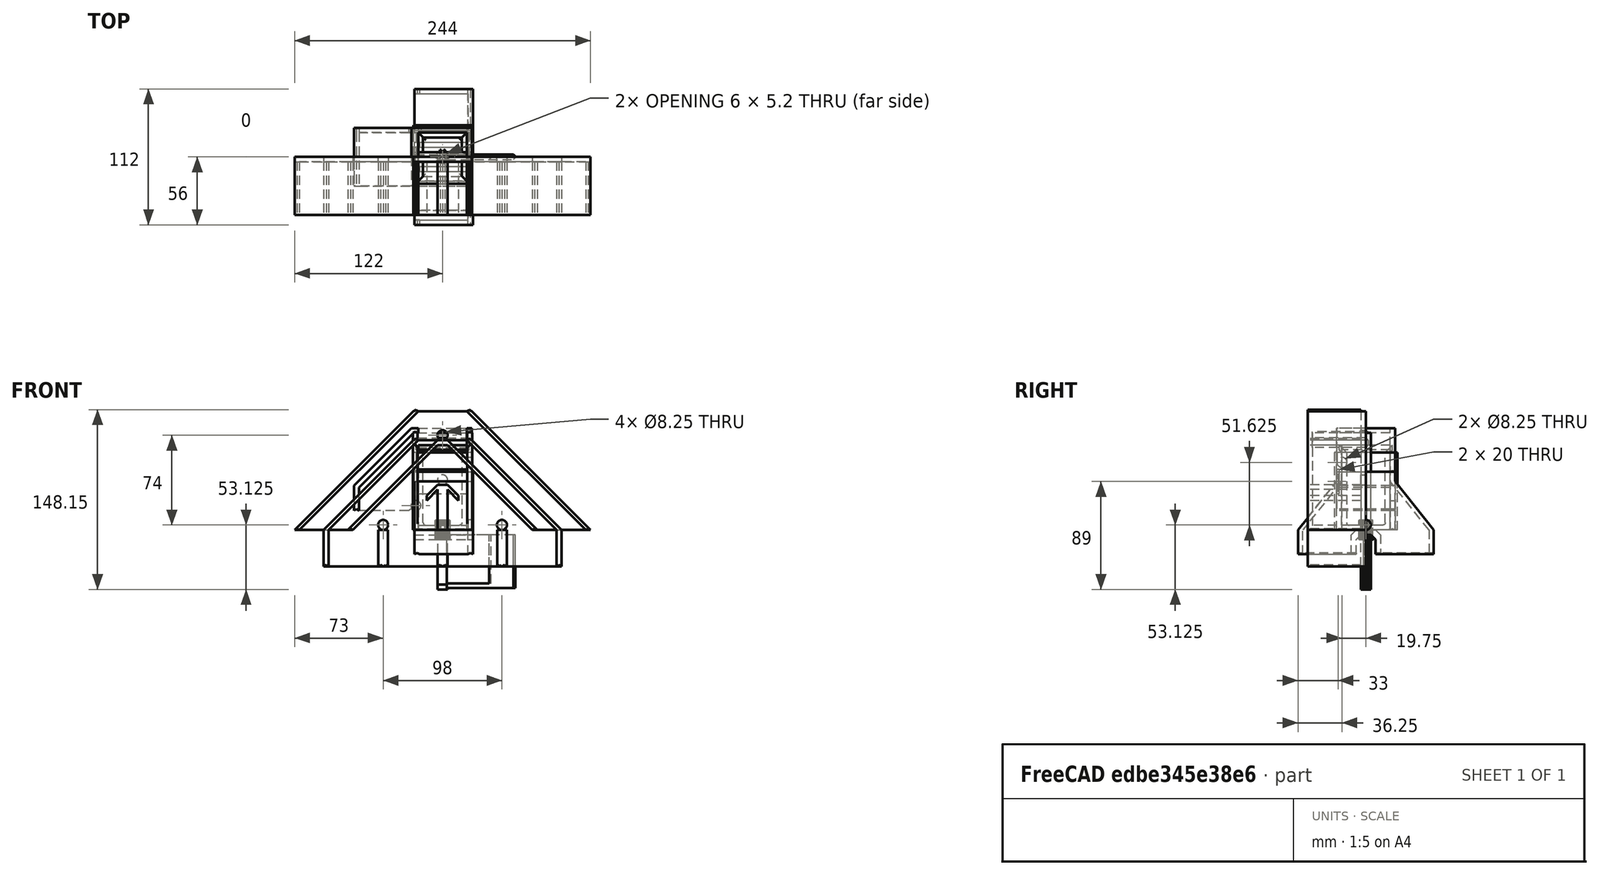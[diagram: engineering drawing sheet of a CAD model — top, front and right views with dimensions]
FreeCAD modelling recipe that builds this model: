
FCSTD DOCUMENT  (FreeCAD 1.0R39319 (Git))
Label: Sorter
License: GNU GPLv3
LicenseURL: https://www.gnu.org/licenses/gpl-3.0.en.html
objects: App::Link×58, Part::Extrusion×27, Sketcher::SketchObject×26, Part::MultiFuse×8, Part::Cut×4, Part::Fuse×2, Part::Fillet×2, Part::Chamfer×2, Spreadsheet::Sheet×1, Part::Part2DObjectPython×1, App::FeaturePython×1, Assembly::JointGroup×1, Assembly::AssemblyObject×1
note: 98 computed .brp shape members not serialized (recipe doc carries the construction recipe); baked Part::Feature solids carry a one-line shape summary decoded from their .brp

FEATURE [Spreadsheet::Sheet] Spreadsheet  label="Variables"
  cells = A1='Bin Width; B1(BinWidth)==40 mm; A2='Bin Height; B2(BinHeight)==60 mm; A3='Wall Width; B3(WallWidth)==4 mm; A4='Tolerance; B4(Tolerance)==1 mm; A5='Connector Angle; B5(ConnectorAngle)==30 deg; A6='Flap Pin Diameter; B6(FlapPinDiameter)==8 mm; A7='Flap Tolerance; B7(FlapTolerance)==0.25 mm
FEATURE [Sketcher::SketchObject] Sketch001
  ArcFitTolerance = 1e-06
  FullyConstrained = true
  MakeInternals = false
  MapMode = 2
  Placement = pos=(0,0,0) rot=(1,0,0;1.5708rad)
  expr: Constraints[16] = <<Variables>>.BinWidth + <<Variables>>.Tolerance
  expr: Constraints[19] = <<Variables>>.WallWidth
  expr: Constraints[20] = <<Variables>>.WallWidth
  expr: Constraints[21] = <<Variables>>.BinHeight + <<Variables>>.WallWidth
  expr: Constraints[30] = <<Variables>>.WallWidth
  expr: Constraints[31] = <<Variables>>.WallWidth
  expr: Constraints[32] = <<Variables>>.WallWidth
  expr: Constraints[33] = <<Variables>>.WallWidth / 2
  expr: Constraints[54] = <<Variables>>.ConnectorAngle
  sketch-geometry (20):
    g0: LineSegment StartX=24.5 StartY=0 StartZ=0 EndX=-24.5 EndY=0 EndZ=0
    g1: LineSegment StartX=-24.5 StartY=0 StartZ=0 EndX=-24.5 EndY=80 EndZ=0
    g2: LineSegment StartX=-20.5 StartY=80 StartZ=0 EndX=-20.5 EndY=76 EndZ=0
    g3: LineSegment StartX=-20.5 StartY=76 StartZ=0 EndX=-22.5 EndY=74 EndZ=0
    g4: LineSegment StartX=-22.5 StartY=74 StartZ=0 EndX=-22.5 EndY=70 EndZ=0
    g5: LineSegment StartX=-22.5 StartY=70 StartZ=0 EndX=-20.5 EndY=68 EndZ=0
    g6: LineSegment StartX=-20.5 StartY=68 StartZ=0 EndX=-20.5 EndY=4 EndZ=0
    g7: LineSegment StartX=-20.5 StartY=4 StartZ=0 EndX=20.5 EndY=4 EndZ=0
    g8: LineSegment StartX=20.5 StartY=4 StartZ=0 EndX=20.5 EndY=68 EndZ=0
    g9: LineSegment StartX=20.5 StartY=68 StartZ=0 EndX=22.5 EndY=70 EndZ=0
    g10: LineSegment StartX=22.5 StartY=70 StartZ=0 EndX=22.5 EndY=74 EndZ=0
    g11: LineSegment StartX=22.5 StartY=74 StartZ=0 EndX=20.5 EndY=76 EndZ=0
    g12: LineSegment StartX=20.5 StartY=76 StartZ=0 EndX=20.5 EndY=80 EndZ=0
    g13: LineSegment StartX=24.5 StartY=80 StartZ=0 EndX=24.5 EndY=0 EndZ=0
    g14: LineSegment StartX=20.5 StartY=80 StartZ=0 EndX=22.5 EndY=81.1547 EndZ=0
    g15: LineSegment StartX=22.5 StartY=81.1547 StartZ=0 EndX=24.5 EndY=80 EndZ=0
    g16: LineSegment [constr] StartX=20.5 StartY=80 StartZ=0 EndX=24.5 EndY=80 EndZ=0
    g17: LineSegment StartX=-24.5 StartY=80 StartZ=0 EndX=-22.5 EndY=81.1547 EndZ=0
    g18: LineSegment StartX=-22.5 StartY=81.1547 StartZ=0 EndX=-20.5 EndY=80 EndZ=0
    g19: LineSegment [constr] StartX=-24.5 StartY=80 StartZ=0 EndX=-20.5 EndY=80 EndZ=0
  constraints (56):
    c: Coincident(g0,g1)
    c: Vertical(g1)
    c: Vertical(g2)
    c: Vertical(g4)
    c: Coincident(g5,g6)
    c: Vertical(g6)
    c: Coincident(g6,g7)
    c: Coincident(g7,g8)
    c: Vertical(g8)
    c: Coincident(g8,g9)
    c: Coincident(g9,g10)
    c: Vertical(g10)
    c: Coincident(g10,g11)
    c: Coincident(g11,g12)
    c: Coincident(g13,g0)
    c: Vertical(g13)
    c: DistanceX(g7,g7) = 41
    c: Symmetric(g0,g0,g-2)
    c: Symmetric(g7,g6,g-2)
    c: DistanceX(g7,g0) = 4
    c: DistanceY(g0,g7) = 4
    c: DistanceY(g8,g8) = 64
    c: Equal(g6,g8)
    c: Equal(g13,g1)
    c: Equal(g2,g12)
    c: Vertical(g12)
    c: Angle(g8,g9) = 2.35619
    c: Angle(g11,g12) = 2.35619
    c: Angle(g5,g6) = 2.35619
    c: Angle(g2,g3) = 2.35619
    c: DistanceX(g12,g13) = 4
    c: DistanceY(g12,g12) = 4
    c: DistanceY(g10,g10) = 4
    c: DistanceX(g9,g13) = 2
    c: Equal(g4,g10)
    c: PointOnObject(g0,g-1)
    c: Coincident(g12,g14)
    c: Coincident(g14,g15)
    c: Coincident(g15,g13)
    c: Equal(g14,g15)
    c: Coincident(g16,g12)
    c: Coincident(g16,g13)
    c: Horizontal(g16)
    c: Coincident(g1,g17)
    c: Coincident(g17,g18)
    c: Coincident(g18,g2)
    c: Equal(g17,g18)
    c: Coincident(g19,g1)
    c: Coincident(g19,g2)
    c: Horizontal(g19)
    c: Coincident(g3,g2)
    c: Coincident(g3,g4)
    c: Coincident(g4,g5)
    c: Equal(g19,g16)
    c: Angle(g19,g17) = 0.523599
    c: Parallel(g14,g17)
FEATURE [Sketcher::SketchObject] Sketch002
  ArcFitTolerance = 1e-06
  AttachmentSupport = -> [Sketch001]
  FullyConstrained = true
  MakeInternals = false
  MapMode = 4
  Placement = pos=(0,0,0) rot=(0.707107,0,0.707107;3.14159rad)
  expr: Constraints[21] = <<Variables>>.WallWidth
  expr: Constraints[22] = <<Variables>>.WallWidth
  expr: Constraints[23] = <<Variables>>.WallWidth / 2
  expr: Constraints[25] = <<Variables>>.BinHeight + <<Variables>>.WallWidth * 2
  expr: Constraints[6] = <<Variables>>.WallWidth
  sketch-geometry (9):
    g0: LineSegment StartX=0 StartY=0 StartZ=0 EndX=0 EndY=-4 EndZ=0
    g1: LineSegment StartX=0 StartY=-4 StartZ=0 EndX=68 EndY=-4 EndZ=0
    g2: LineSegment StartX=68 StartY=0 StartZ=0 EndX=0 EndY=0 EndZ=0
    g3: LineSegment StartX=68 StartY=0 StartZ=0 EndX=70 EndY=-2 EndZ=0
    g4: LineSegment StartX=70 StartY=-2 StartZ=0 EndX=74 EndY=-2 EndZ=0
    g5: LineSegment StartX=74 StartY=-2 StartZ=0 EndX=76 EndY=0 EndZ=0
    g6: LineSegment StartX=76 StartY=0 StartZ=0 EndX=80 EndY=0 EndZ=0
    g7: LineSegment StartX=80 StartY=0 StartZ=0 EndX=80 EndY=-4 EndZ=0
    g8: LineSegment StartX=80 StartY=-4 StartZ=0 EndX=68 EndY=-4 EndZ=0
  constraints (26):
    c: Coincident(g-1,g0)
    c: PointOnObject(g0,g-2)
    c: Coincident(g0,g1)
    c: Horizontal(g1)
    c: PointOnObject(g2,g-1)
    c: Coincident(g2,g0)
    c: DistanceY(g0,g0) = 4
    c: Coincident(g2,g3)
    c: Coincident(g3,g4)
    c: Coincident(g4,g5)
    c: PointOnObject(g5,g-1)
    c: Coincident(g5,g6)
    c: PointOnObject(g6,g-1)
    c: Coincident(g6,g7)
    c: Vertical(g7)
    c: Coincident(g7,g8)
    c: Coincident(g8,g1)
    c: Horizontal(g8)
    c: Horizontal(g4)
    c: Angle(g2,g3) = 2.35619
    c: Angle(g5,g6) = 2.35619
    c: DistanceX(g6,g6) = 4
    c: DistanceX(g4,g4) = 4
    c: DistanceY(g7,g3) = 2
    c: Equal(g2,g1)
    c: DistanceX(g2,g2) = 68
FEATURE [Part::Extrusion] Extrude
  Base = -> Sketch001
  Dir = (0,-1,2e-16)
  DirMode = 2
  FaceMakerClass = Part::FaceMakerBullseye
  FaceMakerMode = 3
  LengthFwd = 46
  LengthRev = 0
  Placement = pos=(0,2,0) rot=(0,0,1;0rad)
  Solid = true
  Symmetric = false
  expr: .Placement.Base.y = <<Variables>>.WallWidth / 2
  expr: LengthFwd = <<Variables>>.BinWidth + <<Variables>>.WallWidth * 1.5
FEATURE [Part::Extrusion] Extrude001
  Base = -> Sketch002
  Dir = (1,0,-2e-16)
  DirMode = 2
  FaceMakerClass = Part::FaceMakerBullseye
  FaceMakerMode = 3
  LengthFwd = 49
  LengthRev = 0
  Solid = true
  Symmetric = true
  expr: LengthFwd = <<Variables>>.BinWidth + <<Variables>>.Tolerance + <<Variables>>.WallWidth * 2
FEATURE [Sketcher::SketchObject] Sketch003
  ArcFitTolerance = 1e-06
  FullyConstrained = true
  MakeInternals = false
  Placement = pos=(0,0,0) rot=(1,0,0;1.5708rad)
  expr: Constraints[11] = <<Variables>>.BinWidth
  expr: Constraints[12] = <<Variables>>.WallWidth
  expr: Constraints[13] = <<Variables>>.WallWidth
  expr: Constraints[16] = <<Variables>>.BinHeight + <<Variables>>.WallWidth
  expr: Constraints[31] = <<Variables>>.WallWidth
  expr: Constraints[33] = <<Variables>>.WallWidth / 2
  sketch-geometry (12):
    g0: LineSegment StartX=-20 StartY=0 StartZ=0 EndX=20 EndY=0 EndZ=0
    g1: LineSegment StartX=20 StartY=0 StartZ=0 EndX=20 EndY=64 EndZ=0
    g2: LineSegment StartX=20 StartY=64 StartZ=0 EndX=22 EndY=66 EndZ=0
    g3: LineSegment StartX=16 StartY=64 StartZ=0 EndX=16 EndY=4 EndZ=0
    g4: LineSegment StartX=16 StartY=4 StartZ=0 EndX=-16 EndY=4 EndZ=0
    g5: LineSegment StartX=-16 StartY=4 StartZ=0 EndX=-16 EndY=64 EndZ=0
    g6: LineSegment StartX=-22 StartY=66 StartZ=0 EndX=-20 EndY=64 EndZ=0
    g7: LineSegment StartX=-20 StartY=64 StartZ=0 EndX=-20 EndY=0 EndZ=0
    g8: LineSegment StartX=22 StartY=66 StartZ=0 EndX=22 EndY=70 EndZ=0
    g9: LineSegment StartX=16 StartY=64 StartZ=0 EndX=22 EndY=70 EndZ=0
    g10: LineSegment StartX=-22 StartY=66 StartZ=0 EndX=-22 EndY=70 EndZ=0
    g11: LineSegment StartX=-22 StartY=70 StartZ=0 EndX=-16 EndY=64 EndZ=0
  constraints (34):
    c: PointOnObject(g0,g-1)
    c: Coincident(g0,g1)
    c: Vertical(g1)
    c: Coincident(g1,g2)
    c: Vertical(g3)
    c: Coincident(g3,g4)
    c: Coincident(g4,g5)
    c: Vertical(g5)
    c: Coincident(g6,g7)
    c: Coincident(g7,g0)
    c: Vertical(g7)
    c: DistanceX(g0,g0) = 40
    c: DistanceY(g0,g4) = 4
    c: DistanceX(g0,g4) = 4
    c: Symmetric(g0,g0,g-2)
    c: Symmetric(g4,g3,g-2)
    c: DistanceY(g1,g1) = 64
    c: Equal(g5,g3)
    c: Equal(g7,g1)
    c: Angle(g1,g2) = 2.35619
    c: Angle(g6,g7) = 2.35619
    c: Coincident(g2,g8)
    c: Vertical(g8)
    c: Coincident(g3,g9)
    c: Coincident(g9,g8)
    c: Coincident(g6,g10)
    c: Vertical(g10)
    c: Coincident(g10,g11)
    c: Coincident(g11,g5)
    c: Angle(g11,g5) = 2.35619
    c: Angle(g3,g9) = 2.35619
    c: DistanceY(g10,g10) = 4
    c: Equal(g9,g11)
    c: DistanceX(g6,g6) = 2
FEATURE [Part::Extrusion] Extrude002
  Base = -> Sketch003
  Dir = (0,-1,2e-16)
  DirMode = 2
  FaceMakerClass = Part::FaceMakerBullseye
  FaceMakerMode = 3
  LengthFwd = 40
  LengthRev = 0
  Solid = true
  Symmetric = true
  expr: LengthFwd = <<Variables>>.BinWidth
FEATURE [Part::Fuse] Fusion  label="Union001"
  Base = -> Extrude
  Tool = -> Extrude001
FEATURE [Sketcher::SketchObject] Sketch004
  ArcFitTolerance = 1e-06
  AttachmentSupport = -> [Extrude002]
  FullyConstrained = true
  MakeInternals = false
  MapMode = 4
  Placement = pos=(0,0,0) rot=(0.57735,0.57735,0.57735;2.0944rad)
  expr: Constraints[17] = <<Variables>>.BinWidth
  expr: Constraints[18] = <<Variables>>.BinHeight + <<Variables>>.WallWidth
  expr: Constraints[19] = <<Variables>>.WallWidth
  expr: Constraints[20] = <<Variables>>.WallWidth
  expr: Constraints[21] = <<Variables>>.WallWidth / 2
  expr: Constraints[30] = <<Variables>>.WallWidth
  sketch-geometry (12):
    g0: LineSegment StartX=20 StartY=0 StartZ=0 EndX=-20 EndY=0 EndZ=0
    g1: LineSegment StartX=-20 StartY=0 StartZ=0 EndX=-20 EndY=64 EndZ=0
    g2: LineSegment StartX=-20 StartY=64 StartZ=0 EndX=-22 EndY=66 EndZ=0
    g3: LineSegment StartX=-16 StartY=64 StartZ=0 EndX=-16 EndY=4 EndZ=0
    g4: LineSegment StartX=-16 StartY=4 StartZ=0 EndX=16 EndY=4 EndZ=0
    g5: LineSegment StartX=16 StartY=4 StartZ=0 EndX=16 EndY=64 EndZ=0
    g6: LineSegment StartX=22 StartY=66 StartZ=0 EndX=20 EndY=64 EndZ=0
    g7: LineSegment StartX=20 StartY=64 StartZ=0 EndX=20 EndY=0 EndZ=0
    g8: LineSegment StartX=-22 StartY=66 StartZ=0 EndX=-22 EndY=70 EndZ=0
    g9: LineSegment StartX=-22 StartY=70 StartZ=0 EndX=-16 EndY=64 EndZ=0
    g10: LineSegment StartX=22 StartY=66 StartZ=0 EndX=22 EndY=70 EndZ=0
    g11: LineSegment StartX=22 StartY=70 StartZ=0 EndX=16 EndY=64 EndZ=0
  constraints (34):
    c: PointOnObject(g0,g-1)
    c: Coincident(g0,g1)
    c: Vertical(g1)
    c: Coincident(g1,g2)
    c: Vertical(g3)
    c: Coincident(g3,g4)
    c: Coincident(g4,g5)
    c: Vertical(g5)
    c: Coincident(g6,g7)
    c: Coincident(g7,g0)
    c: Vertical(g7)
    c: Symmetric(g0,g0,g-2)
    c: Symmetric(g3,g4,g-2)
    c: Angle(g2,g1) = 2.35619
    c: Angle(g7,g6) = 2.35619
    c: Equal(g3,g5)
    c: Equal(g7,g1)
    c: DistanceX(g0,g0) = 40
    c: DistanceY(g7,g7) = 64
    c: DistanceX(g4,g0) = 4
    c: DistanceY(g0,g4) = 4
    c: DistanceX(g2,g1) = 2
    c: Coincident(g2,g8)
    c: Vertical(g8)
    c: Coincident(g8,g9)
    c: Coincident(g9,g3)
    c: Coincident(g6,g10)
    c: Vertical(g10)
    c: Coincident(g10,g11)
    c: Coincident(g11,g5)
    c: DistanceY(g8,g8) = 4
    c: Angle(g9,g3) = 2.35619
    c: Angle(g5,g11) = 2.35619
    c: Equal(g6,g2)
FEATURE [Part::Extrusion] Extrude003
  Base = -> Sketch004
  Dir = (1,0,0)
  DirMode = 2
  FaceMakerClass = Part::FaceMakerBullseye
  FaceMakerMode = 3
  LengthFwd = 40
  LengthRev = 0
  Solid = true
  Symmetric = true
  expr: LengthFwd = <<Variables>>.BinWidth
FEATURE [Part::Fuse] Fusion001  label="Union"
  Base = -> Extrude002
  Tool = -> Extrude003
FEATURE [Part::Fillet] Fillet  label="Bin"
  Base = -> Fusion001
  EdgeLinks = -> Fusion001 [Edge11,Edge21,Edge23,Edge30,Edge31,Edge44,Edge50,Edge51,Edge69,Edge73,Edge75,Edge77]
  Edges = 12 edges r=2: [Edge11,Edge21,Edge23,Edge30,Edge31,Edge44,Edge50,Edge51,Edge69,Edge73,Edge75,Edge77]
FEATURE [Part::Fillet] Fillet001  label="Bin Holder"
  Base = -> Fusion
  EdgeLinks = -> Fusion [Edge72,Edge73,Edge74]
  Edges = 3 edges r=1: [Edge72,Edge73,Edge74]
FEATURE [Sketcher::SketchObject] Sketch
  ArcFitTolerance = 1e-06
  FullyConstrained = true
  MakeInternals = false
  MapMode = 5
  Placement = pos=(0,0,0) rot=(1,0,0;1.5708rad)
  expr: Constraints[144] = <<Variables>>.ConnectorAngle
  expr: Constraints[17] = <<Variables>>.WallWidth
  expr: Constraints[29] = <<Variables>>.BinWidth + <<Variables>>.Tolerance
  expr: Constraints[2] = <<Variables>>.WallWidth * 2
  expr: Constraints[36] = <<Variables>>.WallWidth * 2
  expr: Constraints[82] = <<Variables>>.BinWidth
  expr: Constraints[87] = <<Variables>>.WallWidth
  expr: Constraints[91] = <<Variables>>.BinWidth
  expr: Constraints[95] = <<Variables>>.BinWidth
  sketch-geometry (58):
    g0: LineSegment StartX=-20 StartY=74 StartZ=0 EndX=-94 EndY=1.8e-15 EndZ=0
    g1: LineSegment StartX=24 StartY=74 StartZ=0 EndX=98 EndY=1.8e-15 EndZ=0
    g2: LineSegment StartX=4 StartY=37.3394 StartZ=0 EndX=-4 EndY=37.3394 EndZ=0
    g3: LineSegment StartX=4 StartY=37.3394 StartZ=0 EndX=13.146 EndY=28.1934 EndZ=0
    g4: LineSegment StartX=-4 StartY=37.3394 StartZ=0 EndX=-13.146 EndY=28.1934 EndZ=0
    g5: LineSegment StartX=-24 StartY=74 StartZ=0 EndX=-98 EndY=4.4e-15 EndZ=0
    g6: LineSegment StartX=94 StartY=0 StartZ=0 EndX=20 EndY=74 EndZ=0
    g7: LineSegment StartX=-13.146 StartY=24.1934 StartZ=0 EndX=-4 EndY=33.3394 EndZ=0
    g8: LineSegment StartX=4 StartY=33.3394 StartZ=0 EndX=13.146 EndY=24.1934 EndZ=0
    g9: LineSegment StartX=-13.146 StartY=24.1934 StartZ=0 EndX=-13.146 EndY=28.1934 EndZ=0
    g10: LineSegment StartX=13.146 StartY=28.1934 StartZ=0 EndX=13.146 EndY=24.1934 EndZ=0
    g11: LineSegment [constr] StartX=-94 StartY=1.8e-15 StartZ=0 EndX=-53 EndY=0 EndZ=0
    g12: LineSegment StartX=-53 StartY=0 StartZ=0 EndX=-45 EndY=0 EndZ=0
    g13: LineSegment [constr] StartX=-45 StartY=0 StartZ=0 EndX=-4 EndY=0 EndZ=0
    g14: LineSegment [constr] StartX=4 StartY=0 StartZ=0 EndX=45 EndY=0 EndZ=0
    g15: LineSegment StartX=45 StartY=0 StartZ=0 EndX=53 EndY=0 EndZ=0
    g16: LineSegment StartX=-98 StartY=4.4e-15 StartZ=0 EndX=-98 EndY=-30 EndZ=0
    g17: LineSegment [constr] StartX=-98 StartY=-30 StartZ=0 EndX=-94 EndY=-30 EndZ=0
    g18: LineSegment StartX=-94 StartY=-30 StartZ=0 EndX=-94 EndY=3.6e-15 EndZ=0
    g19: LineSegment StartX=-53 StartY=0 StartZ=0 EndX=-53 EndY=-30 EndZ=0
    g20: LineSegment [constr] StartX=-53 StartY=-30 StartZ=0 EndX=-45 EndY=-30 EndZ=0
    g21: LineSegment StartX=-45 StartY=-30 StartZ=0 EndX=-45 EndY=0 EndZ=0
    g22: LineSegment StartX=-4 StartY=0 StartZ=0 EndX=-4 EndY=-30 EndZ=0
    g23: LineSegment [constr] StartX=-4 StartY=-30 StartZ=0 EndX=4 EndY=-30 EndZ=0
    g24: LineSegment StartX=4 StartY=-30 StartZ=0 EndX=4 EndY=0 EndZ=0
    g25: LineSegment StartX=45 StartY=0 StartZ=0 EndX=45 EndY=-30 EndZ=0
    g26: LineSegment [constr] StartX=45 StartY=-30 StartZ=0 EndX=53 EndY=-30 EndZ=0
    g27: LineSegment StartX=53 StartY=-30 StartZ=0 EndX=53 EndY=0 EndZ=0
    g28: LineSegment StartX=98 StartY=1.8e-15 StartZ=0 EndX=98 EndY=-30 EndZ=0
    g29: LineSegment [constr] StartX=98 StartY=-30 StartZ=0 EndX=94 EndY=-30 EndZ=0
    g30: LineSegment StartX=94 StartY=-30 StartZ=0 EndX=94 EndY=0 EndZ=0
    g31: LineSegment [constr] StartX=-20 StartY=74 StartZ=0 EndX=20 EndY=74 EndZ=0
    g32: LineSegment [constr] StartX=20 StartY=74 StartZ=0 EndX=24 EndY=74 EndZ=0
    g33: LineSegment [constr] StartX=-24 StartY=74 StartZ=0 EndX=-20 EndY=74 EndZ=0
    g34: LineSegment [constr] StartX=4 StartY=37.3394 StartZ=0 EndX=20 EndY=74 EndZ=0
    g35: LineSegment [constr] StartX=53 StartY=0 StartZ=0 EndX=94 EndY=0 EndZ=0
    g36: LineSegment StartX=4 StartY=33.3394 StartZ=0 EndX=4 EndY=0 EndZ=0
    g37: LineSegment StartX=-4 StartY=0 StartZ=0 EndX=-4 EndY=33.3394 EndZ=0
    g38: LineSegment StartX=-98 StartY=-30 StartZ=0 EndX=-96 EndY=-28.8453 EndZ=0
    g39: LineSegment StartX=-96 StartY=-28.8453 StartZ=0 EndX=-94 EndY=-30 EndZ=0
    g40: LineSegment StartX=-53 StartY=-30 StartZ=0 EndX=-51 EndY=-28.8453 EndZ=0
    g41: LineSegment StartX=-51 StartY=-28.8453 StartZ=0 EndX=-49 EndY=-30 EndZ=0
    g42: LineSegment StartX=-49 StartY=-30 StartZ=0 EndX=-47 EndY=-28.8453 EndZ=0
    g43: LineSegment StartX=-47 StartY=-28.8453 StartZ=0 EndX=-45 EndY=-30 EndZ=0
    g44: LineSegment StartX=-4 StartY=-30 StartZ=0 EndX=-2 EndY=-28.8453 EndZ=0
    g45: LineSegment StartX=-2 StartY=-28.8453 StartZ=0 EndX=-1e-16 EndY=-30 EndZ=0
    g46: LineSegment StartX=-1e-16 StartY=-30 StartZ=0 EndX=2 EndY=-28.8453 EndZ=0
    g47: LineSegment StartX=2 StartY=-28.8453 StartZ=0 EndX=4 EndY=-30 EndZ=0
    g48: LineSegment StartX=45 StartY=-30 StartZ=0 EndX=47 EndY=-28.8453 EndZ=0
    g49: LineSegment StartX=47 StartY=-28.8453 StartZ=0 EndX=49 EndY=-30 EndZ=0
    g50: LineSegment StartX=49 StartY=-30 StartZ=0 EndX=51 EndY=-28.8453 EndZ=0
    g51: LineSegment StartX=51 StartY=-28.8453 StartZ=0 EndX=53 EndY=-30 EndZ=0
    g52: LineSegment StartX=94 StartY=-30 StartZ=0 EndX=96 EndY=-28.8453 EndZ=0
    g53: LineSegment StartX=96 StartY=-28.8453 StartZ=0 EndX=98 EndY=-30 EndZ=0
    g54: LineSegment StartX=-24 StartY=74 StartZ=0 EndX=-22 EndY=75.1547 EndZ=0
    g55: LineSegment StartX=-22 StartY=75.1547 StartZ=0 EndX=-20 EndY=74 EndZ=0
    g56: LineSegment StartX=20 StartY=74 StartZ=0 EndX=22 EndY=75.1547 EndZ=0
    g57: LineSegment StartX=22 StartY=75.1547 StartZ=0 EndX=24 EndY=74 EndZ=0
  constraints (154):
    c: PointOnObject(g0,g-1)
    c: PointOnObject(g1,g-1)
    c: DistanceX(g2,g2) = 8
    c: Symmetric(g2,g2,g-2)
    c: Coincident(g3,g2)
    c: Coincident(g4,g2)
    c: Parallel(g4,g0)
    c: Parallel(g3,g1)
    c: Perpendicular(g1,g0)
    c: Equal(g4,g3)
    c: PointOnObject(g5,g-1)
    c: Equal(g5,g0)
    c: Parallel(g0,g5)
    c: PointOnObject(g6,g-1)
    c: Parallel(g1,g6)
    c: Equal(g6,g1)
    c: Symmetric(g7,g8,g-2)
    c: Distance(g7,g2) = 4
    c: Parallel(g7,g4)
    c: Equal(g4,g7)
    c: Equal(g3,g8)
    c: Parallel(g8,g3)
    c: Coincident(g9,g7)
    c: Coincident(g9,g4)
    c: Coincident(g10,g3)
    c: Coincident(g10,g8)
    c: Vertical(g10)
    c: Coincident(g11,g0)
    c: PointOnObject(g11,g-1)
    c: DistanceX(g11,g11) = 41
    c: Coincident(g12,g11)
    c: PointOnObject(g12,g-1)
    c: Coincident(g13,g12)
    c: PointOnObject(g13,g-1)
    c: Symmetric(g13,g14,g-2)
    c: Equal(g11,g13)
    c: DistanceX(g12,g12) = 8
    c: PointOnObject(g14,g-1)
    c: Coincident(g15,g14)
    c: PointOnObject(g15,g-1)
    c: Equal(g14,g11)
    c: Coincident(g5,g16)
    c: Vertical(g16)
    c: Coincident(g16,g17)
    c: Horizontal(g17)
    c: Coincident(g17,g18)
    c: Coincident(g18,g0)
    c: Vertical(g18)
    c: Coincident(g11,g19)
    c: Vertical(g19)
    c: Coincident(g19,g20)
    c: Horizontal(g20)
    c: Coincident(g20,g21)
    c: Coincident(g21,g12)
    c: Vertical(g21)
    c: Coincident(g13,g22)
    c: Vertical(g22)
    c: Coincident(g22,g23)
    c: Horizontal(g23)
    c: Coincident(g23,g24)
    c: Vertical(g24)
    c: Coincident(g14,g25)
    c: Vertical(g25)
    c: Coincident(g25,g26)
    c: Horizontal(g26)
    c: Coincident(g26,g27)
    c: Coincident(g27,g15)
    c: Vertical(g27)
    c: Coincident(g1,g28)
    c: Vertical(g28)
    c: Coincident(g28,g29)
    c: Horizontal(g29)
    c: Coincident(g29,g30)
    c: Coincident(g30,g6)
    c: Vertical(g30)
    c: Equal(g28,g27)
    c: Equal(g25,g24)
    c: Equal(g22,g21)
    c: Equal(g19,g16)
    c: DistanceY(g16,g16) = 30
    c: Coincident(g31,g0)
    c: Coincident(g31,g6)
    c: DistanceX(g31,g31) = 40
    c: Coincident(g32,g6)
    c: Coincident(g32,g1)
    c: Coincident(g33,g5)
    c: Coincident(g33,g0)
    c: DistanceX(g33,g33) = 4
    c: Equal(g33,g32)
    c: Coincident(g34,g2)
    c: Coincident(g34,g6)
    c: Distance(g34,g34) = 40
    c: Coincident(g35,g15)
    c: Coincident(g35,g6)
    c: Equal(g14,g35)
    c: Distance(g8,g14) = 40
    c: Symmetric(g6,g0,g-2)
    c: Coincident(g37,g13)
    c: Coincident(g37,g7)
    c: Coincident(g36,g14)
    c: Coincident(g24,g14)
    c: Vertical(g37)
    c: Equal(g12,g15)
    c: Coincident(g36,g8)
    c: Coincident(g16,g38)
    c: Coincident(g38,g39)
    c: Coincident(g39,g17)
    c: Coincident(g19,g40)
    c: Coincident(g40,g41)
    c: Symmetric(g20,g20,g41)
    c: Coincident(g41,g42)
    c: Coincident(g42,g43)
    c: Coincident(g43,g20)
    c: Coincident(g22,g44)
    c: Coincident(g44,g45)
    c: Symmetric(g23,g23,g45)
    c: Coincident(g45,g46)
    c: Coincident(g46,g47)
    c: Coincident(g47,g23)
    c: Coincident(g25,g48)
    c: Coincident(g48,g49)
    c: Symmetric(g26,g26,g49)
    c: Coincident(g49,g50)
    c: Coincident(g50,g51)
    c: Coincident(g51,g26)
    c: Coincident(g29,g52)
    c: Coincident(g52,g53)
    c: Coincident(g53,g28)
    c: Equal(g52,g53)
    c: Equal(g38,g39)
    c: Equal(g40,g41)
    c: Equal(g42,g43)
    c: Equal(g45,g44)
    c: Equal(g46,g47)
    c: Equal(g48,g49)
    c: Equal(g50,g51)
    c: Coincident(g5,g54)
    c: Coincident(g54,g55)
    c: Coincident(g55,g0)
    c: Coincident(g6,g56)
    c: Coincident(g56,g57)
    c: Coincident(g57,g1)
    c: Equal(g56,g57)
    c: Equal(g55,g54)
    c: Angle(g33,g54) = 0.523599
    c: Parallel(g52,g50)
    c: Parallel(g50,g48)
    c: Parallel(g48,g46)
    c: Parallel(g46,g44)
    c: Parallel(g44,g42)
    c: Parallel(g42,g40)
    c: Parallel(g40,g38)
    c: Parallel(g52,g54)
    c: Parallel(g56,g54)
FEATURE [Part::Extrusion] Extrude004
  Base = -> Sketch
  Dir = (0,-1,2e-16)
  DirMode = 2
  FaceMakerClass = Part::FaceMakerBullseye
  FaceMakerMode = 3
  LengthFwd = 44
  LengthRev = 0
  Placement = pos=(0,-4,0) rot=(0,0,1;0rad)
  Solid = true
  Symmetric = false
  expr: .Placement.Base.y = -<<Variables>>.WallWidth
  expr: LengthFwd = <<Variables>>.BinWidth + <<Variables>>.WallWidth
FEATURE [Sketcher::SketchObject] Sketch005
  ArcFitTolerance = 1e-06
  FullyConstrained = true
  MakeInternals = false
  MapMode = 5
  Placement = pos=(0,0,0) rot=(1,0,0;1.5708rad)
  expr: Constraints[122] = <<Variables>>.ConnectorAngle
  expr: Constraints[131] = <<Variables>>.WallWidth
  expr: Constraints[132] = (<<Variables>>.FlapPinDiameter + <<Variables>>.FlapTolerance) / 2
  expr: Constraints[133] = <<Variables>>.FlapPinDiameter + <<Variables>>.FlapTolerance
  expr: Constraints[13] = <<Variables>>.WallWidth * 2
  expr: Constraints[158] = <<Variables>>.BinWidth
  expr: Constraints[159] = <<Variables>>.BinWidth
  expr: Constraints[162] = <<Variables>>.FlapPinDiameter / 2
  expr: Constraints[26] = <<Variables>>.WallWidth
  expr: Constraints[31] = <<Variables>>.BinWidth
  expr: Constraints[4] = <<Variables>>.BinWidth + <<Variables>>.Tolerance
  sketch-geometry (60):
    g0: LineSegment StartX=24 StartY=74 StartZ=0 EndX=98 EndY=1.8e-15 EndZ=0
    g1: LineSegment StartX=-24 StartY=74 StartZ=0 EndX=-98 EndY=1.8e-15 EndZ=0
    g2: LineSegment [constr] StartX=-94 StartY=0 StartZ=0 EndX=-53 EndY=0 EndZ=0
    g3: LineSegment [constr] StartX=-53 StartY=0 StartZ=0 EndX=-45 EndY=0 EndZ=0
    g4: LineSegment [constr] StartX=-45 StartY=0 StartZ=0 EndX=-4 EndY=0 EndZ=0
    g5: LineSegment [constr] StartX=-4 StartY=0 StartZ=0 EndX=4 EndY=0 EndZ=0
    g6: LineSegment [constr] StartX=4 StartY=0 StartZ=0 EndX=45 EndY=0 EndZ=0
    g7: LineSegment [constr] StartX=45 StartY=0 StartZ=0 EndX=53 EndY=0 EndZ=0
    g8: LineSegment StartX=-98 StartY=1.8e-15 StartZ=0 EndX=-98 EndY=-30 EndZ=0
    g9: LineSegment StartX=98 StartY=1.8e-15 StartZ=0 EndX=98 EndY=-30 EndZ=0
    g10: LineSegment StartX=20 StartY=74 StartZ=0 EndX=24 EndY=74 EndZ=0
    g11: LineSegment StartX=-24 StartY=74 StartZ=0 EndX=-20 EndY=74 EndZ=0
    g12: LineSegment StartX=-20 StartY=74 StartZ=0 EndX=20 EndY=74 EndZ=0
    g13: LineSegment [constr] StartX=-94 StartY=0 StartZ=0 EndX=-98 EndY=1.8e-15 EndZ=0
    g14: LineSegment [constr] StartX=53 StartY=0 StartZ=0 EndX=94 EndY=0 EndZ=0
    g15: LineSegment [constr] StartX=94 StartY=0 StartZ=0 EndX=98 EndY=1.8e-15 EndZ=0
    g16: LineSegment [constr] StartX=-98 StartY=-30 StartZ=0 EndX=-96 EndY=-28.8453 EndZ=0
    g17: LineSegment [constr] StartX=-96 StartY=-28.8453 StartZ=0 EndX=-94 EndY=-30 EndZ=0
    g18: LineSegment StartX=-94 StartY=-30 StartZ=0 EndX=-53 EndY=-30 EndZ=0
    g19: LineSegment [constr] StartX=-53 StartY=-30 StartZ=0 EndX=-51 EndY=-28.8453 EndZ=0
    g20: LineSegment [constr] StartX=-51 StartY=-28.8453 StartZ=0 EndX=-49 EndY=-30 EndZ=0
    g21: LineSegment [constr] StartX=-49 StartY=-30 StartZ=0 EndX=-47 EndY=-28.8453 EndZ=0
    g22: LineSegment [constr] StartX=-47 StartY=-28.8453 StartZ=0 EndX=-45 EndY=-30 EndZ=0
    g23: LineSegment StartX=-45 StartY=-30 StartZ=0 EndX=-4 EndY=-30 EndZ=0
    g24: LineSegment [constr] StartX=-4 StartY=-30 StartZ=0 EndX=-2 EndY=-28.8453 EndZ=0
    g25: LineSegment [constr] StartX=-2 StartY=-28.8453 StartZ=0 EndX=-1e-16 EndY=-30 EndZ=0
    g26: LineSegment [constr] StartX=-1e-16 StartY=-30 StartZ=0 EndX=2 EndY=-28.8453 EndZ=0
    g27: LineSegment [constr] StartX=2 StartY=-28.8453 StartZ=0 EndX=4 EndY=-30 EndZ=0
    g28: LineSegment StartX=4 StartY=-30 StartZ=0 EndX=45 EndY=-30 EndZ=0
    g29: LineSegment [constr] StartX=45 StartY=-30 StartZ=0 EndX=47 EndY=-28.8453 EndZ=0
    g30: LineSegment [constr] StartX=47 StartY=-28.8453 StartZ=0 EndX=49 EndY=-30 EndZ=0
    g31: LineSegment [constr] StartX=49 StartY=-30 StartZ=0 EndX=51 EndY=-28.8453 EndZ=0
    g32: LineSegment [constr] StartX=51 StartY=-28.8453 StartZ=0 EndX=53 EndY=-30 EndZ=0
    g33: LineSegment StartX=53 StartY=-30 StartZ=0 EndX=94 EndY=-30 EndZ=0
    g34: LineSegment [constr] StartX=94 StartY=-30 StartZ=0 EndX=96 EndY=-28.8453 EndZ=0
    g35: LineSegment [constr] StartX=96 StartY=-28.8453 StartZ=0 EndX=98 EndY=-30 EndZ=0
    g36: LineSegment StartX=98 StartY=-30 StartZ=0 EndX=94 EndY=-30 EndZ=0
    g37: LineSegment StartX=53 StartY=-30 StartZ=0 EndX=49 EndY=-30 EndZ=0
    g38: LineSegment StartX=49 StartY=-30 StartZ=0 EndX=45 EndY=-30 EndZ=0
    g39: LineSegment StartX=-1e-16 StartY=-30 StartZ=0 EndX=-4 EndY=-30 EndZ=0
    g40: LineSegment StartX=-1e-16 StartY=-30 StartZ=0 EndX=4 EndY=-30 EndZ=0
    g41: LineSegment StartX=-45 StartY=-30 StartZ=0 EndX=-49 EndY=-30 EndZ=0
    g42: LineSegment StartX=-53 StartY=-30 StartZ=0 EndX=-49 EndY=-30 EndZ=0
    g43: LineSegment StartX=-98 StartY=-30 StartZ=0 EndX=-94 EndY=-30 EndZ=0
    g44: LineSegment [constr] StartX=-24 StartY=74 StartZ=0 EndX=-22 EndY=75.1547 EndZ=0
    g45: LineSegment [constr] StartX=-22 StartY=75.1547 StartZ=0 EndX=-20 EndY=74 EndZ=0
    g46: LineSegment [constr] StartX=20 StartY=74 StartZ=0 EndX=22 EndY=75.1547 EndZ=0
    g47: LineSegment [constr] StartX=22 StartY=75.1547 StartZ=0 EndX=24 EndY=74 EndZ=0
    g48: Circle CenterX=-49 CenterY=4.125 CenterZ=0 NormalX=0 NormalY=0 NormalZ=1 AngleXU=0 Radius=4.125
    g49: Circle CenterX=49 CenterY=4.125 CenterZ=0 NormalX=0 NormalY=0 NormalZ=1 AngleXU=0 Radius=4.125
    g50: Circle CenterX=0 CenterY=41.3394 CenterZ=0 NormalX=0 NormalY=0 NormalZ=1 AngleXU=0 Radius=4.125
    g51: LineSegment [constr] StartX=4 StartY=37.3394 StartZ=0 EndX=-4 EndY=37.3394 EndZ=0
    g52: LineSegment [constr] StartX=4 StartY=37.3394 StartZ=0 EndX=13.146 EndY=28.1934 EndZ=0
    g53: LineSegment [constr] StartX=-4 StartY=37.3394 StartZ=0 EndX=-13.146 EndY=28.1934 EndZ=0
    g54: LineSegment [constr] StartX=-13.146 StartY=24.1934 StartZ=0 EndX=-4 EndY=33.3394 EndZ=0
    g55: LineSegment [constr] StartX=4 StartY=33.3394 StartZ=0 EndX=13.146 EndY=24.1934 EndZ=0
    g56: LineSegment [constr] StartX=-13.146 StartY=24.1934 StartZ=0 EndX=-13.146 EndY=28.1934 EndZ=0
    g57: LineSegment [constr] StartX=13.146 StartY=28.1934 StartZ=0 EndX=13.146 EndY=24.1934 EndZ=0
    g58: LineSegment [constr] StartX=4 StartY=33.3394 StartZ=0 EndX=4 EndY=0 EndZ=0
    g59: LineSegment [constr] StartX=-4 StartY=0 StartZ=0 EndX=-4 EndY=33.3394 EndZ=0
  constraints (163):
    c: PointOnObject(g2,g-1)
    c: PointOnObject(g0,g-1)
    c: PointOnObject(g1,g-1)
    c: PointOnObject(g2,g-1)
    c: DistanceX(g2,g2) = 41
    c: Coincident(g3,g2)
    c: PointOnObject(g3,g-1)
    c: Coincident(g4,g3)
    c: PointOnObject(g4,g-1)
    c: Coincident(g5,g4)
    c: Symmetric(g4,g5,g-2)
    c: Equal(g3,g5)
    c: Equal(g2,g4)
    c: DistanceX(g3,g3) = 8
    c: Coincident(g6,g5)
    c: PointOnObject(g6,g-1)
    c: Coincident(g7,g6)
    c: PointOnObject(g7,g-1)
    c: Equal(g6,g2)
    c: Coincident(g1,g8)
    c: Vertical(g8)
    c: Coincident(g0,g9)
    c: Vertical(g9)
    c: DistanceY(g8,g8) = 30
    c: Coincident(g10,g0)
    c: Coincident(g11,g1)
    c: DistanceX(g11,g11) = 4
    c: Equal(g11,g10)
    c: Coincident(g12,g11)
    c: Coincident(g12,g10)
    c: Horizontal(g10)
    c: DistanceX(g12,g12) = 40
    c: Horizontal(g11)
    c: Symmetric(g11,g10,g-2)
    c: Equal(g7,g5)
    c: Perpendicular(g0,g1)
    c: Coincident(g13,g2)
    c: Coincident(g13,g1)
    c: Coincident(g14,g7)
    c: PointOnObject(g14,g-1)
    c: Coincident(g15,g14)
    c: Coincident(g15,g0)
    c: Equal(g14,g6)
    c: Equal(g15,g10)
    c: Equal(g11,g13)
    c: Coincident(g8,g16)
    c: Coincident(g16,g17)
    c: Coincident(g17,g18)
    c: Horizontal(g18)
    c: Coincident(g18,g19)
    c: Coincident(g19,g20)
    c: Coincident(g20,g21)
    c: Coincident(g21,g22)
    c: Coincident(g22,g23)
    c: Horizontal(g23)
    c: Coincident(g23,g24)
    c: Coincident(g24,g25)
    c: PointOnObject(g25,g-2)
    c: Coincident(g25,g26)
    c: Coincident(g26,g27)
    c: Coincident(g27,g28)
    c: Horizontal(g28)
    c: Coincident(g28,g29)
    c: Coincident(g29,g30)
    c: Coincident(g30,g31)
    c: Coincident(g31,g32)
    c: Coincident(g32,g33)
    c: Horizontal(g33)
    c: Coincident(g33,g34)
    c: Coincident(g34,g35)
    c: Coincident(g35,g9)
    c: Coincident(g36,g9)
    c: Coincident(g36,g33)
    c: Coincident(g37,g32)
    c: Coincident(g37,g30)
    c: Coincident(g38,g30)
    c: Coincident(g38,g28)
    c: Coincident(g39,g25)
    c: Coincident(g39,g23)
    c: Coincident(g40,g25)
    c: Coincident(g40,g27)
    c: Coincident(g41,g22)
    c: Coincident(g41,g20)
    c: Coincident(g42,g18)
    c: Coincident(g42,g20)
    c: Coincident(g43,g8)
    c: Coincident(g43,g17)
    c: Horizontal(g43)
    c: Horizontal(g42)
    c: Horizontal(g41)
    c: Horizontal(g39)
    c: Horizontal(g40)
    c: Horizontal(g38)
    c: Horizontal(g37)
    c: Horizontal(g36)
    c: Equal(g13,g43)
    c: Equal(g43,g42)
    c: Equal(g41,g42)
    c: Equal(g41,g39)
    c: Equal(g39,g40)
    c: Equal(g40,g38)
    c: Equal(g38,g37)
    c: Equal(g37,g36)
    c: Equal(g34,g35)
    c: Equal(g32,g31)
    c: Equal(g30,g29)
    c: Equal(g27,g26)
    c: Equal(g25,g24)
    c: Equal(g22,g21)
    c: Equal(g20,g19)
    c: Equal(g17,g16)
    c: Equal(g14,g33)
    c: Equal(g33,g18)
    c: Coincident(g1,g44)
    c: Coincident(g44,g45)
    c: Coincident(g45,g11)
    c: Coincident(g10,g46)
    c: Coincident(g46,g47)
    c: Coincident(g47,g0)
    c: Equal(g45,g44)
    c: Equal(g46,g47)
    c: Parallel(g44,g46)
    c: Angle(g11,g44) = 0.523599
    c: Parallel(g34,g46)
    c: Parallel(g34,g31)
    c: Parallel(g31,g29)
    c: Parallel(g29,g26)
    c: Parallel(g26,g24)
    c: Parallel(g24,g21)
    c: Parallel(g21,g19)
    c: Parallel(g19,g16)
    c: DistanceX(g48,g3) = 4
    c: DistanceY(g2,g48) = 4.125
    c: Diameter(g48) = 8.25
    c: Equal(g49,g48)
    c: Symmetric(g48,g49,g-2)
    c: PointOnObject(g50,g-2)
    c: Equal(g50,g48)
    c: DistanceX(g51,g51) = 8
    c: Symmetric(g51,g51,g-2)
    c: Coincident(g52,g51)
    c: Coincident(g53,g51)
    c: Equal(g53,g52)
    c: Symmetric(g54,g55,g-2)
    c: Distance(g54,g51) = 4
    c: Parallel(g54,g53)
    c: Equal(g53,g54)
    c: Equal(g52,g55)
    c: Parallel(g55,g52)
    c: Coincident(g56,g54)
    c: Coincident(g56,g53)
    c: Coincident(g57,g52)
    c: Coincident(g57,g55)
    c: Vertical(g57)
    c: Coincident(g59,g54)
    c: Coincident(g58,g55)
    c: Coincident(g59,g4)
    c: Coincident(g58,g5)
    c: Distance(g55,g6) = 40
    c: Distance(g10,g51) = 40
    c: Parallel(g1,g53)
    c: Parallel(g52,g0)
    c: Distance(g50,g51) = 4
FEATURE [Part::Extrusion] Extrude007
  Base = -> Sketch005
  Dir = (0,-1,2e-16)
  DirMode = 2
  FaceMakerClass = Part::FaceMakerBullseye
  FaceMakerMode = 3
  LengthFwd = 4
  LengthRev = 0
  Solid = true
  Symmetric = false
  expr: LengthFwd = <<Variables>>.WallWidth
FEATURE [Sketcher::SketchObject] Sketch006
  ArcFitTolerance = 1e-06
  FullyConstrained = true
  MakeInternals = false
  Placement = pos=(0,0,0) rot=(1,0,0;1.5708rad)
  expr: Constraints[14] = <<Variables>>.WallWidth * 2
  expr: Constraints[17] = <<Variables>>.BinWidth * 3 + <<Variables>>.WallWidth * 7
  expr: Constraints[18] = <<Variables>>.BinWidth
  expr: Constraints[21] = <<Variables>>.BinWidth
  expr: Constraints[28] = <<Variables>>.WallWidth
  expr: Constraints[37] = <<Variables>>.WallWidth
  expr: Constraints[52] = <<Variables>>.ConnectorAngle
  sketch-geometry (32):
    g0: LineSegment StartX=-20 StartY=98 StartZ=0 EndX=-118 EndY=1e-15 EndZ=0
    g1: LineSegment StartX=118 StartY=0 StartZ=0 EndX=20 EndY=98 EndZ=0
    g2: LineSegment StartX=-4 StartY=70 StartZ=0 EndX=-74 EndY=3.6e-15 EndZ=0
    g3: LineSegment StartX=-4 StartY=74 StartZ=0 EndX=4 EndY=74 EndZ=0
    g4: LineSegment StartX=74 StartY=0 StartZ=0 EndX=4 EndY=70 EndZ=0
    g5: LineSegment StartX=4 StartY=70 StartZ=0 EndX=-4 EndY=70 EndZ=0
    g6: LineSegment [constr] StartX=20 StartY=98 StartZ=0 EndX=4 EndY=70 EndZ=0
    g7: LineSegment [constr] StartX=-74 StartY=3.6e-15 StartZ=0 EndX=74 EndY=0 EndZ=0
    g8: LineSegment [constr] StartX=-118 StartY=1.2e-15 StartZ=0 EndX=-78 EndY=3.6e-15 EndZ=0
    g9: LineSegment [constr] StartX=-20 StartY=98 StartZ=0 EndX=20 EndY=98 EndZ=0
    g10: LineSegment [constr] StartX=-24 StartY=98 StartZ=0 EndX=-20 EndY=98 EndZ=0
    g11: LineSegment [constr] StartX=20 StartY=98 StartZ=0 EndX=24 EndY=98 EndZ=0
    g12: LineSegment StartX=-122 StartY=0 StartZ=0 EndX=-24 EndY=98 EndZ=0
    g13: LineSegment [constr] StartX=-118 StartY=1.2e-15 StartZ=0 EndX=-122 EndY=0 EndZ=0
    g14: LineSegment [constr] StartX=-74 StartY=3.6e-15 StartZ=0 EndX=-78 EndY=3.6e-15 EndZ=0
    g15: LineSegment StartX=-4 StartY=74 StartZ=0 EndX=-78 EndY=1.8e-15 EndZ=0
    g16: LineSegment [constr] StartX=74 StartY=0 StartZ=0 EndX=78 EndY=0 EndZ=0
    g17: LineSegment StartX=78 StartY=0 StartZ=0 EndX=4 EndY=74 EndZ=0
    g18: LineSegment [constr] StartX=118 StartY=0 StartZ=0 EndX=122 EndY=0 EndZ=0
    g19: LineSegment StartX=122 StartY=0 StartZ=0 EndX=24 EndY=98 EndZ=0
    g20: LineSegment StartX=-24 StartY=98 StartZ=0 EndX=-22 EndY=99.1547 EndZ=0
    g21: LineSegment StartX=-22 StartY=99.1547 StartZ=0 EndX=-20 EndY=98 EndZ=0
    g22: LineSegment StartX=20 StartY=98 StartZ=0 EndX=22 EndY=99.1547 EndZ=0
    g23: LineSegment StartX=22 StartY=99.1547 StartZ=0 EndX=24 EndY=98 EndZ=0
    g24: LineSegment StartX=-122 StartY=0 StartZ=0 EndX=-120 EndY=1.1547 EndZ=0
    g25: LineSegment StartX=-120 StartY=1.1547 StartZ=0 EndX=-118 EndY=1.2e-15 EndZ=0
    g26: LineSegment StartX=-78 StartY=3.6e-15 StartZ=0 EndX=-76 EndY=1.1547 EndZ=0
    g27: LineSegment StartX=-76 StartY=1.1547 StartZ=0 EndX=-74 EndY=3.6e-15 EndZ=0
    g28: LineSegment StartX=78 StartY=0 StartZ=0 EndX=76 EndY=1.1547 EndZ=0
    g29: LineSegment StartX=76 StartY=1.1547 StartZ=0 EndX=74 EndY=0 EndZ=0
    g30: LineSegment StartX=118 StartY=0 StartZ=0 EndX=120 EndY=1.1547 EndZ=0
    g31: LineSegment StartX=120 StartY=1.1547 StartZ=0 EndX=122 EndY=0 EndZ=0
  constraints (84):
    c: PointOnObject(g0,g-1)
    c: PointOnObject(g1,g-1)
    c: Perpendicular(g1,g0)
    c: Equal(g0,g1)
    c: Symmetric(g0,g1,g-2)
    c: PointOnObject(g2,g-1)
    c: Horizontal(g3)
    c: PointOnObject(g4,g-1)
    c: Coincident(g4,g5)
    c: Coincident(g5,g2)
    c: Equal(g5,g3)
    c: Parallel(g4,g1)
    c: Parallel(g2,g0)
    c: Symmetric(g2,g4,g-2)
    c: DistanceX(g5,g5) = 8
    c: Coincident(g6,g4)
    c: Coincident(g7,g2)
    c: DistanceX(g7,g7) = 148
    c: DistanceX(g8,g8) = 40
    c: Coincident(g9,g0)
    c: Coincident(g9,g6)
    c: DistanceX(g9,g9) = 40
    c: Coincident(g1,g6)
    c: Coincident(g10,g0)
    c: Horizontal(g10)
    c: Coincident(g11,g1)
    c: Horizontal(g11)
    c: Equal(g10,g11)
    c: DistanceX(g10,g10) = 4
    c: Coincident(g12,g10)
    c: Coincident(g13,g0)
    c: PointOnObject(g13,g-1)
    c: Equal(g13,g10)
    c: Coincident(g0,g8)
    c: Coincident(g14,g8)
    c: Horizontal(g14)
    c: Coincident(g15,g8)
    c: DistanceX(g14,g14) = 4
    c: PointOnObject(g16,g-1)
    c: Coincident(g16,g17)
    c: Coincident(g4,g7)
    c: PointOnObject(g18,g-1)
    c: Coincident(g19,g11)
    c: Parallel(g19,g1)
    c: Coincident(g18,g1)
    c: Coincident(g10,g20)
    c: Coincident(g20,g21)
    c: Coincident(g21,g0)
    c: Coincident(g1,g22)
    c: Coincident(g22,g23)
    c: Coincident(g23,g11)
    c: Coincident(g16,g4) = 30
    c: Angle(g10,g20) = 0.523599
    c: Parallel(g22,g20)
    c: Equal(g20,g21)
    c: Equal(g22,g23)
    c: Coincident(g13,g24)
    c: Coincident(g24,g25)
    c: Coincident(g25,g0)
    c: Parallel(g24,g20)
    c: Equal(g24,g25)
    c: Coincident(g12,g13)
    c: Coincident(g8,g26)
    c: Coincident(g26,g27)
    c: Coincident(g27,g14)
    c: Parallel(g26,g24)
    c: Equal(g26,g27)
    c: Coincident(g14,g2)
    c: Coincident(g16,g28)
    c: Coincident(g28,g29)
    c: Coincident(g29,g4)
    c: Parallel(g29,g26)
    c: Equal(g29,g28)
    c: Equal(g16,g14)
    c: Coincident(g1,g30)
    c: Coincident(g30,g31)
    c: Coincident(g31,g18)
    c: Equal(g30,g31)
    c: Parallel(g30,g29)
    c: Coincident(g19,g18)
    c: Coincident(g15,g3)
    c: Coincident(g17,g3)
    c: Parallel(g15,g2)
    c: Parallel(g17,g4)
FEATURE [Sketcher::SketchObject] Sketch007
  ArcFitTolerance = 1e-06
  FullyConstrained = true
  MakeInternals = false
  Placement = pos=(0,0,0) rot=(1,0,0;1.5708rad)
  expr: Constraints[10] = <<Variables>>.WallWidth
  expr: Constraints[20] = <<Variables>>.WallWidth * 2
  expr: Constraints[25] = <<Variables>>.BinWidth
  expr: Constraints[27] = <<Variables>>.BinWidth * 3 + <<Variables>>.WallWidth * 7
  expr: Constraints[28] = <<Variables>>.BinWidth
  expr: Constraints[44] = <<Variables>>.WallWidth
  expr: Constraints[66] = <<Variables>>.ConnectorAngle
  expr: Constraints[86] = <<Variables>>.FlapPinDiameter + <<Variables>>.FlapTolerance
  expr: Constraints[87] = (<<Variables>>.FlapPinDiameter + <<Variables>>.FlapTolerance) / 2
  sketch-geometry (34):
    g0: LineSegment StartX=-24 StartY=98 StartZ=0 EndX=-20 EndY=98 EndZ=0
    g1: LineSegment [constr] StartX=-20 StartY=98 StartZ=0 EndX=-118 EndY=6.9e-15 EndZ=0
    g2: LineSegment StartX=20 StartY=98 StartZ=0 EndX=24 EndY=98 EndZ=0
    g3: LineSegment [constr] StartX=118 StartY=0 StartZ=0 EndX=20 EndY=98 EndZ=0
    g4: LineSegment StartX=-4 StartY=70 StartZ=0 EndX=-74 EndY=-1.5e-15 EndZ=0
    g5: LineSegment [constr] StartX=-4 StartY=74 StartZ=0 EndX=4 EndY=74 EndZ=0
    g6: LineSegment StartX=74 StartY=2e-16 StartZ=0 EndX=4 EndY=70 EndZ=0
    g7: LineSegment StartX=4 StartY=70 StartZ=0 EndX=-4 EndY=70 EndZ=0
    g8: LineSegment StartX=-20 StartY=98 StartZ=0 EndX=20 EndY=98 EndZ=0
    g9: LineSegment [constr] StartX=20 StartY=98 StartZ=0 EndX=4 EndY=70 EndZ=0
    g10: LineSegment StartX=-118 StartY=6.9e-15 StartZ=0 EndX=-78 EndY=6.9e-15 EndZ=0
    g11: LineSegment [constr] StartX=-74 StartY=-1.5e-15 StartZ=0 EndX=74 EndY=2e-16 EndZ=0
    g12: LineSegment StartX=78 StartY=2e-16 StartZ=0 EndX=118 EndY=0 EndZ=0
    g13: LineSegment StartX=122 StartY=0 StartZ=0 EndX=24 EndY=98 EndZ=0
    g14: LineSegment StartX=118 StartY=0 StartZ=0 EndX=122 EndY=0 EndZ=0
    g15: LineSegment StartX=74 StartY=2e-16 StartZ=0 EndX=78 EndY=2e-16 EndZ=0
    g16: LineSegment StartX=-78 StartY=6.9e-15 StartZ=0 EndX=-74 EndY=6.9e-15 EndZ=0
    g17: LineSegment [constr] StartX=-78 StartY=6.9e-15 StartZ=0 EndX=-4 EndY=74 EndZ=0
    g18: LineSegment [constr] StartX=4 StartY=74 StartZ=0 EndX=78 EndY=1.8e-15 EndZ=0
    g19: LineSegment StartX=-24 StartY=98 StartZ=0 EndX=-122 EndY=6.9e-15 EndZ=0
    g20: LineSegment [constr] StartX=-24 StartY=98 StartZ=0 EndX=-22 EndY=99.1547 EndZ=0
    g21: LineSegment [constr] StartX=-22 StartY=99.1547 StartZ=0 EndX=-20 EndY=98 EndZ=0
    g22: LineSegment [constr] StartX=20 StartY=98 StartZ=0 EndX=22 EndY=99.1547 EndZ=0
    g23: LineSegment [constr] StartX=22 StartY=99.1547 StartZ=0 EndX=24 EndY=98 EndZ=0
    g24: LineSegment [constr] StartX=-122 StartY=6.9e-15 StartZ=0 EndX=-120 EndY=1.1547 EndZ=0
    g25: LineSegment [constr] StartX=-120 StartY=1.1547 StartZ=0 EndX=-118 EndY=6.8e-15 EndZ=0
    g26: LineSegment [constr] StartX=-78 StartY=6.9e-15 StartZ=0 EndX=-76 EndY=1.1547 EndZ=0
    g27: LineSegment [constr] StartX=-76 StartY=1.1547 StartZ=0 EndX=-74 EndY=6.8e-15 EndZ=0
    g28: LineSegment [constr] StartX=74 StartY=2e-16 StartZ=0 EndX=76 EndY=1.1547 EndZ=0
    g29: LineSegment [constr] StartX=76 StartY=1.1547 StartZ=0 EndX=78 EndY=2e-16 EndZ=0
    g30: LineSegment [constr] StartX=118 StartY=0 StartZ=0 EndX=120 EndY=1.1547 EndZ=0
    g31: LineSegment [constr] StartX=120 StartY=1.1547 StartZ=0 EndX=122 EndY=0 EndZ=0
    g32: Circle CenterX=0 CenterY=78.125 CenterZ=0 NormalX=0 NormalY=0 NormalZ=1 AngleXU=0 Radius=4.125
    g33: LineSegment StartX=-122 StartY=6.9e-15 StartZ=0 EndX=-118 EndY=6.9e-15 EndZ=0
  constraints (90):
    c: PointOnObject(g1,g-1)
    c: Horizontal(g0)
    c: Coincident(g0,g1)
    c: Horizontal(g2)
    c: PointOnObject(g3,g-1)
    c: Coincident(g3,g2)
    c: Perpendicular(g3,g1)
    c: Equal(g1,g3)
    c: Equal(g0,g2)
    c: Symmetric(g0,g2,g-2)
    c: DistanceX(g0,g0) = 4
    c: PointOnObject(g4,g-1)
    c: Horizontal(g5)
    c: PointOnObject(g6,g-1)
    c: Coincident(g6,g7)
    c: Coincident(g7,g4)
    c: Equal(g7,g5)
    c: Parallel(g6,g3)
    c: Parallel(g4,g1)
    c: Symmetric(g4,g6,g-2)
    c: DistanceX(g7,g7) = 8
    c: Coincident(g8,g0)
    c: Coincident(g8,g2)
    c: Coincident(g9,g2)
    c: Coincident(g9,g6)
    c: DistanceX(g8,g8) = 40
    c: Coincident(g11,g4)
    c: DistanceX(g11,g11) = 148
    c: DistanceX(g10,g10) = 40
    c: Coincident(g13,g2)
    c: PointOnObject(g14,g-1)
    c: Parallel(g13,g3)
    c: Coincident(g12,g3)
    c: Coincident(g15,g12)
    c: Horizontal(g15)
    c: Coincident(g16,g10)
    c: Horizontal(g16)
    c: Coincident(g17,g5)
    c: Coincident(g18,g5)
    c: Coincident(g6,g11)
    c: Parallel(g17,g4)
    c: Coincident(g19,g0)
    c: Parallel(g19,g1)
    c: Coincident(g10,g1)
    c: DistanceX(g16,g16) = 4
    c: Equal(g16,g15)
    c: Coincident(g0,g20)
    c: Coincident(g20,g21)
    c: Coincident(g21,g0)
    c: Coincident(g2,g22)
    c: Coincident(g22,g23)
    c: Coincident(g23,g2)
    c: Equal(g21,g20)
    c: Equal(g22,g23)
    c: Coincident(g17,g10)
    c: Coincident(g18,g12)
    c: Coincident(g15,g6)
    c: Coincident(g13,g14)
    c: Coincident(g3,g14)
    c: Equal(g12,g10)
    c: PointOnObject(g19,g-1)
    c: Horizontal(g10)
    c: Coincident(g19,g24)
    c: Coincident(g24,g25)
    c: Coincident(g25,g1)
    c: Equal(g24,g25)
    c: Angle(g0,g20) = 0.523599
    c: Parallel(g22,g20)
    c: Parallel(g20,g24)
    c: Parallel(g18,g6)
    c: Coincident(g10,g26)
    c: Coincident(g26,g27)
    c: Coincident(g27,g16)
    c: Coincident(g28,g29)
    c: Coincident(g29,g12)
    c: Coincident(g3,g30)
    c: Coincident(g30,g31)
    c: Coincident(g31,g13)
    c: Equal(g31,g30)
    c: Equal(g28,g29)
    c: Equal(g26,g27)
    c: Parallel(g24,g26)
    c: Parallel(g26,g28)
    c: Parallel(g28,g30)
    c: Coincident(g28,g6)
    c: PointOnObject(g32,g-2)
    c: Diameter(g32) = 8.25
    c: DistanceY(g5,g32) = 4.125
    c: Coincident(g33,g19)
    c: Coincident(g33,g1)
FEATURE [Part::Extrusion] Extrude008
  Base = -> Sketch006
  Dir = (0,-1,2e-16)
  DirMode = 2
  FaceMakerClass = Part::FaceMakerBullseye
  FaceMakerMode = 3
  LengthFwd = 44
  LengthRev = 0
  Placement = pos=(0,-4,0) rot=(0,0,1;0rad)
  Solid = true
  Symmetric = false
  expr: .Placement.Base.y = -<<Variables>>.WallWidth
FEATURE [Part::Extrusion] Extrude009
  Base = -> Sketch007
  Dir = (0,-1,2e-16)
  DirMode = 2
  FaceMakerClass = Part::FaceMakerBullseye
  FaceMakerMode = 3
  LengthFwd = 4
  LengthRev = 0
  Solid = true
  Symmetric = false
  expr: LengthFwd = <<Variables>>.WallWidth
FEATURE [Part::MultiFuse] Fusion002  label="Stage 2 Paths"
  Shapes = -> [Extrude008,Extrude009]
FEATURE [Sketcher::SketchObject] Sketch009
  ArcFitTolerance = 1e-06
  FullyConstrained = true
  MakeInternals = false
  MapMode = 5
  Placement = pos=(0,0,0) rot=(0.57735,0.57735,0.57735;2.0944rad)
  expr: Constraints[33] = <<Variables>>.WallWidth
  expr: Constraints[43] = <<Variables>>.BinWidth
  expr: Constraints[44] = <<Variables>>.BinWidth
  expr: Constraints[45] = <<Variables>>.WallWidth * 5
  expr: Constraints[49] = <<Variables>>.BinWidth
  expr: Constraints[55] = (<<Variables>>.FlapPinDiameter + <<Variables>>.FlapTolerance) / 2
  expr: Constraints[56] = <<Variables>>.FlapPinDiameter + <<Variables>>.FlapTolerance
  expr: Constraints[63] = <<Variables>>.WallWidth
  expr: Constraints[64] = <<Variables>>.WallWidth
  expr: Constraints[68] = <<Variables>>.WallWidth * 2
  expr: Constraints[79] = <<Variables>>.WallWidth * 4
  expr: Constraints[81] = <<Variables>>.WallWidth
  sketch-geometry (31):
    g0: LineSegment StartX=-56 StartY=0 StartZ=0 EndX=-24 EndY=40 EndZ=0
    g1: LineSegment [constr] StartX=-24 StartY=40 StartZ=0 EndX=-20 EndY=40 EndZ=0
    g2: LineSegment [constr] StartX=-20 StartY=40 StartZ=0 EndX=-52 EndY=-2.1e-15 EndZ=0
    g3: LineSegment [constr] StartX=52 StartY=0 StartZ=0 EndX=20 EndY=40 EndZ=0
    g4: LineSegment [constr] StartX=20 StartY=40 StartZ=0 EndX=24 EndY=40 EndZ=0
    g5: LineSegment StartX=24 StartY=40 StartZ=0 EndX=56 EndY=-1.9e-15 EndZ=0
    g6: LineSegment StartX=-56 StartY=0 StartZ=0 EndX=-56 EndY=-20 EndZ=0
    g7: LineSegment StartX=-56 StartY=-20 StartZ=0 EndX=-52 EndY=-20 EndZ=0
    g8: LineSegment [constr] StartX=-52 StartY=-20 StartZ=0 EndX=-52 EndY=-3.6e-15 EndZ=0
    g9: LineSegment [constr] StartX=52 StartY=0 StartZ=0 EndX=52 EndY=-20 EndZ=0
    g10: LineSegment StartX=52 StartY=-20 StartZ=0 EndX=56 EndY=-20 EndZ=0
    g11: LineSegment StartX=56 StartY=-20 StartZ=0 EndX=56 EndY=-3.6e-15 EndZ=0
    g12: LineSegment [constr] StartX=-12 StartY=0 StartZ=0 EndX=12 EndY=0 EndZ=0
    g13: LineSegment [constr] StartX=12 StartY=0 StartZ=0 EndX=12 EndY=-20 EndZ=0
    g14: LineSegment [constr] StartX=-12 StartY=-20 StartZ=0 EndX=-12 EndY=0 EndZ=0
    g15: LineSegment [constr] StartX=-20 StartY=40 StartZ=0 EndX=20 EndY=40 EndZ=0
    g16: LineSegment [constr] StartX=-52 StartY=-2.1e-15 StartZ=0 EndX=-12 EndY=0 EndZ=0
    g17: LineSegment [constr] StartX=12 StartY=0 StartZ=0 EndX=52 EndY=0 EndZ=0
    g18: LineSegment StartX=-52 StartY=-20 StartZ=0 EndX=-12 EndY=-20 EndZ=0
    g19: LineSegment StartX=12 StartY=-20 StartZ=0 EndX=52 EndY=-20 EndZ=0
    g20: LineSegment StartX=-24 StartY=48 StartZ=0 EndX=24 EndY=48 EndZ=0
    g21: LineSegment StartX=24 StartY=48 StartZ=0 EndX=24 EndY=40 EndZ=0
    g22: Circle CenterX=0 CenterY=4.125 CenterZ=0 NormalX=0 NormalY=0 NormalZ=1 AngleXU=0 Radius=4.125
    g23: LineSegment StartX=-12 StartY=-20 StartZ=0 EndX=-8 EndY=-20 EndZ=0
    g24: LineSegment StartX=-4 StartY=-4 StartZ=0 EndX=4 EndY=-4 EndZ=0
    g25: LineSegment StartX=8 StartY=-20 StartZ=0 EndX=12 EndY=-20 EndZ=0
    g26: LineSegment StartX=-24 StartY=40 StartZ=0 EndX=-24 EndY=48 EndZ=0
    g27: LineSegment StartX=-8 StartY=-20 StartZ=0 EndX=-8 EndY=-8 EndZ=0
    g28: LineSegment StartX=-8 StartY=-8 StartZ=0 EndX=-4 EndY=-4 EndZ=0
    g29: LineSegment StartX=4 StartY=-4 StartZ=0 EndX=8 EndY=-8 EndZ=0
    g30: LineSegment StartX=8 StartY=-8 StartZ=0 EndX=8 EndY=-20 EndZ=0
  constraints (83):
    c: PointOnObject(g2,g-1)
    c: PointOnObject(g0,g-1)
    c: Coincident(g0,g1)
    c: Coincident(g1,g2)
    c: PointOnObject(g5,g-1)
    c: Coincident(g3,g4)
    c: Coincident(g4,g5)
    c: Horizontal(g4)
    c: Horizontal(g1)
    c: Equal(g4,g1)
    c: Parallel(g2,g0)
    c: Parallel(g3,g5)
    c: Coincident(g0,g6)
    c: Vertical(g6)
    c: Coincident(g6,g7)
    c: Horizontal(g7)
    c: Coincident(g7,g8)
    c: Coincident(g8,g2)
    c: Coincident(g3,g9)
    c: Vertical(g9)
    c: Coincident(g9,g10)
    c: Horizontal(g10)
    c: Coincident(g10,g11)
    c: Coincident(g11,g5)
    c: Vertical(g11)
    c: Vertical(g8)
    c: PointOnObject(g12,g-1)
    c: Coincident(g12,g13)
    c: Vertical(g13)
    c: Coincident(g14,g12)
    c: Vertical(g14)
    c: Equal(g13,g9)
    c: Equal(g14,g8)
    c: DistanceX(g1,g1) = 4
    c: Symmetric(g1,g3,g-2)
    c: Symmetric(g2,g3,g-2)
    c: Symmetric(g12,g12,g-2)
    c: Coincident(g15,g1)
    c: Coincident(g15,g3)
    c: Coincident(g16,g2)
    c: Coincident(g16,g12)
    c: Coincident(g17,g12)
    c: Coincident(g17,g3)
    c: DistanceX(g15,g15) = 40
    c: DistanceX(g16,g16) = 40
    c: DistanceY(g11,g11) = 20
    c: Coincident(g18,g7)
    c: Coincident(g19,g13)
    c: Coincident(g19,g9)
    c: Distance(g3,g17) = 40
    c: Horizontal(g20)
    c: Coincident(g20,g21)
    c: Coincident(g21,g4)
    c: Vertical(g21)
    c: PointOnObject(g22,g-2)
    c: DistanceY(g12,g22) = 4.125
    c: Diameter(g22) = 8.25
    c: Coincident(g18,g23)
    c: Horizontal(g23)
    c: Coincident(g25,g13)
    c: Horizontal(g25)
    c: Equal(g25,g23)
    c: Coincident(g18,g14)
    c: DistanceX(g23,g23) = 4
    c: Distance(g24,g12) = 4
    c: Coincident(g26,g0)
    c: Coincident(g26,g20)
    c: Vertical(g26)
    c: DistanceY(g26,g26) = 8
    c: Coincident(g23,g27)
    c: Vertical(g27)
    c: Coincident(g27,g28)
    c: Coincident(g28,g24)
    c: Coincident(g24,g29)
    c: Coincident(g29,g30)
    c: Coincident(g30,g25)
    c: Vertical(g30)
    c: Perpendicular(g29,g28)
    c: Symmetric(g24,g24,g-2)
    c: DistanceX(g27,g29) = 16
    c: Angle(g27,g28) = 2.35619
    c: DistanceX(g27,g24) = 4
    c: Equal(g27,g30)
FEATURE [Part::Extrusion] Extrude011
  Base = -> Sketch009
  Dir = (1,0,0)
  DirMode = 2
  FaceMakerClass = Part::FaceMakerBullseye
  FaceMakerMode = 3
  LengthFwd = 4
  LengthRev = 0
  Placement = pos=(22,0,0) rot=(0,0,1;0rad)
  Solid = true
  Symmetric = false
  expr: LengthFwd = <<Variables>>.WallWidth
FEATURE [Sketcher::SketchObject] Sketch008
  ArcFitTolerance = 1e-06
  FullyConstrained = true
  MakeInternals = false
  MapMode = 5
  Placement = pos=(0,0,0) rot=(0.57735,0.57735,0.57735;2.0944rad)
  expr: Constraints[104] = <<Variables>>.WallWidth * 4
  expr: Constraints[27] = <<Variables>>.WallWidth
  expr: Constraints[35] = <<Variables>>.BinWidth
  expr: Constraints[36] = <<Variables>>.BinWidth
  expr: Constraints[37] = <<Variables>>.WallWidth * 5
  expr: Constraints[38] = <<Variables>>.BinWidth
  expr: Constraints[52] = <<Variables>>.WallWidth * 2
  expr: Constraints[59] = <<Variables>>.ConnectorAngle
  expr: Constraints[63] = <<Variables>>.WallWidth
  expr: Constraints[93] = <<Variables>>.WallWidth
  sketch-geometry (40):
    g0: LineSegment StartX=-56 StartY=0 StartZ=0 EndX=-24 EndY=40 EndZ=0
    g1: LineSegment [constr] StartX=-24 StartY=40 StartZ=0 EndX=-20 EndY=40 EndZ=0
    g2: LineSegment StartX=-20 StartY=40 StartZ=0 EndX=-52 EndY=-2.1e-15 EndZ=0
    g3: LineSegment StartX=52 StartY=0 StartZ=0 EndX=20 EndY=40 EndZ=0
    g4: LineSegment [constr] StartX=20 StartY=40 StartZ=0 EndX=24 EndY=40 EndZ=0
    g5: LineSegment StartX=24 StartY=40 StartZ=0 EndX=56 EndY=-2.1e-15 EndZ=0
    g6: LineSegment StartX=-56 StartY=0 StartZ=0 EndX=-56 EndY=-20 EndZ=0
    g7: LineSegment StartX=-56 StartY=-20 StartZ=0 EndX=-52 EndY=-20 EndZ=0
    g8: LineSegment StartX=-52 StartY=-20 StartZ=0 EndX=-52 EndY=-3.6e-15 EndZ=0
    g9: LineSegment StartX=52 StartY=0 StartZ=0 EndX=52 EndY=-20 EndZ=0
    g10: LineSegment StartX=52 StartY=-20 StartZ=0 EndX=56 EndY=-20 EndZ=0
    g11: LineSegment StartX=56 StartY=-20 StartZ=0 EndX=56 EndY=-3.6e-15 EndZ=0
    g12: LineSegment [constr] StartX=-20 StartY=40 StartZ=0 EndX=20 EndY=40 EndZ=0
    g13: LineSegment [constr] StartX=-52 StartY=-2.1e-15 StartZ=0 EndX=-12 EndY=0 EndZ=0
    g14: LineSegment [constr] StartX=12 StartY=0 StartZ=0 EndX=52 EndY=0 EndZ=0
    g15: LineSegment StartX=-24 StartY=40 StartZ=0 EndX=-24 EndY=48 EndZ=0
    g16: LineSegment StartX=-24 StartY=48 StartZ=0 EndX=-20 EndY=48 EndZ=0
    g17: LineSegment StartX=-20 StartY=48 StartZ=0 EndX=-20 EndY=40 EndZ=0
    g18: LineSegment StartX=20 StartY=40 StartZ=0 EndX=20 EndY=48 EndZ=0
    g19: LineSegment [constr] StartX=20 StartY=48 StartZ=0 EndX=24 EndY=48 EndZ=0
    g20: LineSegment StartX=24 StartY=48 StartZ=0 EndX=24 EndY=40 EndZ=0
    g21: LineSegment StartX=20 StartY=48 StartZ=0 EndX=22 EndY=49.1547 EndZ=0
    g22: LineSegment StartX=22 StartY=49.1547 StartZ=0 EndX=24 EndY=48 EndZ=0
    g23: LineSegment StartX=-8 StartY=-20 StartZ=0 EndX=-12 EndY=-20 EndZ=0
    g24: LineSegment StartX=12 StartY=-20 StartZ=0 EndX=8 EndY=-20 EndZ=0
    g25: LineSegment StartX=-4 StartY=-4 StartZ=0 EndX=4 EndY=-4 EndZ=0
    g26: LineSegment StartX=12 StartY=-4 StartZ=0 EndX=12 EndY=-20 EndZ=0
    g27: LineSegment StartX=-12 StartY=-20 StartZ=0 EndX=-12 EndY=-4 EndZ=0
    g28: LineSegment [constr] StartX=-12 StartY=-20 StartZ=0 EndX=-52 EndY=-20 EndZ=0
    g29: LineSegment StartX=-12 StartY=-4 StartZ=0 EndX=-8 EndY=-1e-16 EndZ=0
    g30: LineSegment StartX=-8 StartY=-1e-16 StartZ=0 EndX=8 EndY=0 EndZ=0
    g31: LineSegment StartX=8 StartY=0 StartZ=0 EndX=12 EndY=-4 EndZ=0
    g32: LineSegment [constr] StartX=-12 StartY=0 StartZ=0 EndX=-8 EndY=-1e-16 EndZ=0
    g33: LineSegment [constr] StartX=8 StartY=0 StartZ=0 EndX=12 EndY=0 EndZ=0
    g34: LineSegment [constr] StartX=-12 StartY=0 StartZ=0 EndX=-12 EndY=-4 EndZ=0
    g35: LineSegment [constr] StartX=12 StartY=0 StartZ=0 EndX=12 EndY=-4 EndZ=0
    g36: LineSegment StartX=-8 StartY=-20 StartZ=0 EndX=-8 EndY=-8 EndZ=0
    g37: LineSegment StartX=-8 StartY=-8 StartZ=0 EndX=-4 EndY=-4 EndZ=0
    g38: LineSegment StartX=4 StartY=-4 StartZ=0 EndX=8 EndY=-8 EndZ=0
    g39: LineSegment StartX=8 StartY=-8 StartZ=0 EndX=8 EndY=-20 EndZ=0
  constraints (108):
    c: PointOnObject(g2,g-1)
    c: PointOnObject(g0,g-1)
    c: Coincident(g0,g1)
    c: Coincident(g1,g2)
    c: PointOnObject(g5,g-1)
    c: Coincident(g3,g4)
    c: Coincident(g4,g5)
    c: Horizontal(g4)
    c: Horizontal(g1)
    c: Equal(g4,g1)
    c: Parallel(g2,g0)
    c: Parallel(g3,g5)
    c: Coincident(g0,g6)
    c: Vertical(g6)
    c: Coincident(g6,g7)
    c: Horizontal(g7)
    c: Coincident(g7,g8)
    c: Coincident(g8,g2)
    c: Coincident(g3,g9)
    c: Vertical(g9)
    c: Coincident(g9,g10)
    c: Horizontal(g10)
    c: Coincident(g10,g11)
    c: Coincident(g11,g5)
    c: Vertical(g11)
    c: Vertical(g8)
    c: PointOnObject(g13,g-1)
    c: DistanceX(g1,g1) = 4
    c: Symmetric(g1,g3,g-2)
    c: Symmetric(g2,g3,g-2)
    c: Symmetric(g13,g14,g-2)
    c: Coincident(g12,g1)
    c: Coincident(g12,g3)
    c: Coincident(g13,g2)
    c: Coincident(g14,g3)
    c: DistanceX(g12,g12) = 40
    c: DistanceX(g13,g13) = 40
    c: DistanceY(g11,g11) = 20
    c: Distance(g3,g14) = 40
    c: Vertical(g15)
    c: Coincident(g15,g16)
    c: Horizontal(g16)
    c: Coincident(g16,g17)
    c: Coincident(g17,g1)
    c: Vertical(g17)
    c: Coincident(g3,g18)
    c: Vertical(g18)
    c: Coincident(g18,g19)
    c: Horizontal(g19)
    c: Coincident(g19,g20)
    c: Coincident(g20,g4)
    c: Vertical(g20)
    c: DistanceY(g15,g15) = 8
    c: Equal(g17,g18)
    c: Coincident(g15,g0)
    c: Coincident(g18,g21)
    c: Coincident(g21,g22)
    c: Coincident(g22,g19)
    c: Equal(g21,g22)
    c: Angle(g19,g21) = 0.523599
    c: Horizontal(g24)
    c: Horizontal(g23)
    c: Equal(g23,g24)
    c: DistanceX(g23,g23) = 4
    c: Horizontal(g25)
    c: Coincident(g26,g24)
    c: Coincident(g23,g27)
    c: Vertical(g27)
    c: Coincident(g28,g23)
    c: Coincident(g28,g7)
    c: Horizontal(g28)
    c: Equal(g6,g11)
    c: Vertical(g26)
    c: Coincident(g27,g29)
    c: PointOnObject(g29,g-1)
    c: Coincident(g29,g30)
    c: PointOnObject(g30,g-1)
    c: Coincident(g30,g31)
    c: Coincident(g31,g26)
    c: Coincident(g32,g13)
    c: Coincident(g32,g29)
    c: Coincident(g33,g30)
    c: Coincident(g33,g14)
    c: Equal(g32,g23)
    c: Equal(g32,g33)
    c: Coincident(g34,g13)
    c: Coincident(g34,g27)
    c: Vertical(g34)
    c: Coincident(g35,g14)
    c: Coincident(g35,g26)
    c: Vertical(g35)
    c: Angle(g31,g33) = 0.785398
    c: Equal(g29,g31)
    c: DistanceY(g25,g29) = 4
    c: Coincident(g23,g36)
    c: Vertical(g36)
    c: Coincident(g36,g37)
    c: Coincident(g37,g25)
    c: Coincident(g25,g38)
    c: Coincident(g38,g39)
    c: Coincident(g39,g24)
    c: Vertical(g39)
    c: Parallel(g38,g31)
    c: Parallel(g37,g29)
    c: DistanceX(g36,g38) = 16
    c: Equal(g39,g36)
    c: Equal(g38,g37)
    c: Equal(g38,g31)
FEATURE [Part::Extrusion] Extrude010
  Base = -> Sketch008
  Dir = (1,0,0)
  DirMode = 2
  FaceMakerClass = Part::FaceMakerBullseye
  FaceMakerMode = 3
  LengthFwd = 44
  LengthRev = 0
  Solid = true
  Symmetric = true
  expr: LengthFwd = <<Variables>>.BinWidth + <<Variables>>.WallWidth
FEATURE [Sketcher::SketchObject] Sketch010
  ArcFitTolerance = 1e-06
  FullyConstrained = true
  MakeInternals = false
  Placement = pos=(0,0,0) rot=(1,0,0;1.5708rad)
  expr: Constraints[15] = <<Variables>>.WallWidth
  expr: Constraints[18] = <<Variables>>.BinWidth
  expr: Constraints[39] = <<Variables>>.WallWidth
  expr: Constraints[40] = <<Variables>>.BinWidth + <<Variables>>.Tolerance + <<Variables>>.WallWidth
  expr: Constraints[41] = <<Variables>>.WallWidth
  expr: Constraints[48] = <<Variables>>.ConnectorAngle
  expr: Constraints[49] = <<Variables>>.WallWidth * 4
  expr: Constraints[53] = <<Variables>>.WallWidth
  expr: Constraints[56] = <<Variables>>.BinHeight + <<Variables>>.FlapPinDiameter / 2
  expr: Constraints[57] = <<Variables>>.WallWidth
  sketch-geometry (22):
    g0: LineSegment StartX=24 StartY=0 StartZ=0 EndX=20 EndY=0 EndZ=0
    g1: LineSegment StartX=20 StartY=0 StartZ=0 EndX=20 EndY=84 EndZ=0
    g2: LineSegment StartX=20 StartY=84 StartZ=0 EndX=24 EndY=84 EndZ=0
    g3: LineSegment StartX=24 StartY=84 StartZ=0 EndX=24 EndY=0 EndZ=0
    g4: LineSegment StartX=-24 StartY=0 StartZ=0 EndX=-20 EndY=0 EndZ=0
    g5: LineSegment StartX=-20 StartY=0 StartZ=0 EndX=-20 EndY=16 EndZ=0
    g6: LineSegment StartX=-20 StartY=16 StartZ=0 EndX=-24 EndY=16 EndZ=0
    g7: LineSegment [constr] StartX=-20 StartY=0 StartZ=0 EndX=20 EndY=0 EndZ=0
    g8: LineSegment StartX=-20 StartY=84 StartZ=0 EndX=-25.6569 EndY=84 EndZ=0
    g9: LineSegment StartX=-24 StartY=80 StartZ=0 EndX=-20 EndY=80 EndZ=0
    g10: LineSegment StartX=-20 StartY=80 StartZ=0 EndX=-20 EndY=84 EndZ=0
    g11: LineSegment [constr] StartX=-20 StartY=84 StartZ=0 EndX=20 EndY=84 EndZ=0
    g12: LineSegment StartX=-25.6569 StartY=84 StartZ=0 EndX=-73 EndY=36.6569 EndZ=0
    g13: LineSegment StartX=-73 StartY=36.6569 StartZ=0 EndX=-73 EndY=16 EndZ=0
    g14: LineSegment [constr] StartX=-73 StartY=16 StartZ=0 EndX=-69 EndY=16 EndZ=0
    g15: LineSegment StartX=-69 StartY=16 StartZ=0 EndX=-69 EndY=35 EndZ=0
    g16: LineSegment StartX=-69 StartY=35 StartZ=0 EndX=-24 EndY=80 EndZ=0
    g17: LineSegment StartX=-24 StartY=16 StartZ=0 EndX=-24 EndY=0 EndZ=0
    g18: LineSegment StartX=-73 StartY=16 StartZ=0 EndX=-71 EndY=17.1547 EndZ=0
    g19: LineSegment StartX=-71 StartY=17.1547 StartZ=0 EndX=-69 EndY=16 EndZ=0
    g20: LineSegment [constr] StartX=-69 StartY=16 StartZ=0 EndX=-24 EndY=16 EndZ=0
    g21: LineSegment [constr] StartX=-20 StartY=16 StartZ=0 EndX=-20 EndY=80 EndZ=0
  constraints (58):
    c: PointOnObject(g0,g-1)
    c: PointOnObject(g0,g-1)
    c: Coincident(g0,g1)
    c: Vertical(g1)
    c: Coincident(g1,g2)
    c: Horizontal(g2)
    c: Coincident(g2,g3)
    c: Coincident(g3,g0)
    c: Vertical(g3)
    c: PointOnObject(g4,g-1)
    c: Coincident(g4,g5)
    c: Vertical(g5)
    c: Coincident(g5,g6)
    c: Horizontal(g6)
    c: Symmetric(g4,g0,g-2)
    c: DistanceX(g2,g2) = 4
    c: Coincident(g7,g4)
    c: Coincident(g7,g0)
    c: DistanceX(g7,g7) = 40
    c: Equal(g6,g0)
    c: Horizontal(g9)
    c: Coincident(g9,g10)
    c: Coincident(g10,g8)
    c: Tangent(g10,g5)
    c: Tangent(g8,g2)
    c: Coincident(g11,g8)
    c: Coincident(g11,g1)
    c: Equal(g6,g4)
    c: Coincident(g12,g8)
    c: Coincident(g13,g12)
    c: Vertical(g13)
    c: Angle(g13,g12) = 2.35619
    c: Coincident(g13,g14)
    c: Horizontal(g14)
    c: Coincident(g14,g15)
    c: Vertical(g15)
    c: Coincident(g15,g16)
    c: Coincident(g16,g9)
    c: Parallel(g16,g12)
    c: DistanceX(g14,g14) = 4
    c: DistanceX(g14,g6) = 45
    c: Distance(g15,g12) = 4
    c: Coincident(g17,g6)
    c: Coincident(g17,g4)
    c: Coincident(g13,g18)
    c: Coincident(g18,g19)
    c: Coincident(g19,g14)
    c: Equal(g19,g18)
    c: Angle(g14,g18) = 0.523599
    c: DistanceY(g5,g5) = 16
    c: Coincident(g20,g14)
    c: Coincident(g20,g6)
    c: Horizontal(g20)
    c: DistanceY(g10,g10) = 4
    c: Coincident(g21,g5)
    c: Coincident(g21,g9)
    c: DistanceY(g21,g21) = 64
    c: DistanceX(g9,g9) = 4
FEATURE [Sketcher::SketchObject] Sketch011
  ArcFitTolerance = 1e-06
  FullyConstrained = true
  MakeInternals = false
  Placement = pos=(0,0,0) rot=(1,0,0;1.5708rad)
  expr: Constraints[15] = <<Variables>>.WallWidth
  expr: Constraints[18] = <<Variables>>.BinWidth
  expr: Constraints[29] = <<Variables>>.BinHeight + <<Variables>>.FlapPinDiameter / 2
  expr: Constraints[30] = <<Variables>>.WallWidth * 4
  expr: Constraints[43] = <<Variables>>.WallWidth
  expr: Constraints[44] = <<Variables>>.BinWidth + <<Variables>>.Tolerance + <<Variables>>.WallWidth
  expr: Constraints[45] = <<Variables>>.WallWidth
  expr: Constraints[62] = <<Variables>>.ConnectorAngle
  expr: Constraints[64] = <<Variables>>.WallWidth / 2
  expr: Constraints[65] = (<<Variables>>.FlapPinDiameter + <<Variables>>.FlapTolerance) / 2
  expr: Constraints[66] = <<Variables>>.FlapPinDiameter + <<Variables>>.FlapTolerance
  expr: Constraints[67] = <<Variables>>.WallWidth
  expr: Constraints[68] = <<Variables>>.WallWidth
  sketch-geometry (26):
    g0: LineSegment StartX=24 StartY=0 StartZ=0 EndX=20 EndY=0 EndZ=0
    g1: LineSegment [constr] StartX=20 StartY=0 StartZ=0 EndX=20 EndY=84 EndZ=0
    g2: LineSegment StartX=20 StartY=84 StartZ=0 EndX=24 EndY=84 EndZ=0
    g3: LineSegment StartX=24 StartY=84 StartZ=0 EndX=24 EndY=0 EndZ=0
    g4: LineSegment StartX=-24 StartY=0 StartZ=0 EndX=-20 EndY=0 EndZ=0
    g5: LineSegment [constr] StartX=-20 StartY=0 StartZ=0 EndX=-20 EndY=16 EndZ=0
    g6: LineSegment [constr] StartX=-20 StartY=16 StartZ=0 EndX=-24 EndY=16 EndZ=0
    g7: LineSegment StartX=-20 StartY=0 StartZ=0 EndX=20 EndY=0 EndZ=0
    g8: LineSegment StartX=-20 StartY=84 StartZ=0 EndX=-25.6569 EndY=84 EndZ=0
    g9: LineSegment [constr] StartX=-24 StartY=80 StartZ=0 EndX=-20 EndY=80 EndZ=0
    g10: LineSegment [constr] StartX=-20 StartY=80 StartZ=0 EndX=-20 EndY=84 EndZ=0
    g11: LineSegment [constr] StartX=-20 StartY=80 StartZ=0 EndX=-20 EndY=16 EndZ=0
    g12: LineSegment StartX=-20 StartY=84 StartZ=0 EndX=20 EndY=84 EndZ=0
    g13: LineSegment StartX=-25.6569 StartY=84 StartZ=0 EndX=-73 EndY=36.6569 EndZ=0
    g14: LineSegment StartX=-73 StartY=36.6569 StartZ=0 EndX=-73 EndY=16 EndZ=0
    g15: LineSegment [constr] StartX=-73 StartY=16 StartZ=0 EndX=-69 EndY=16 EndZ=0
    g16: LineSegment [constr] StartX=-69 StartY=16 StartZ=0 EndX=-69 EndY=35 EndZ=0
    g17: LineSegment [constr] StartX=-69 StartY=35 StartZ=0 EndX=-24 EndY=80 EndZ=0
    g18: LineSegment StartX=-24 StartY=16 StartZ=0 EndX=-24 EndY=0 EndZ=0
    g19: LineSegment StartX=-73 StartY=16 StartZ=0 EndX=-71 EndY=17.1547 EndZ=0
    g20: LineSegment StartX=-69 StartY=16 StartZ=0 EndX=-71 EndY=17.1547 EndZ=0
    g21: LineSegment StartX=-24 StartY=16 StartZ=0 EndX=-26 EndY=17.1547 EndZ=0
    g22: LineSegment StartX=-26 StartY=17.1547 StartZ=0 EndX=-28 EndY=16 EndZ=0
    g23: LineSegment [constr] StartX=-28 StartY=16 StartZ=0 EndX=-24 EndY=16 EndZ=0
    g24: LineSegment StartX=-28 StartY=16 StartZ=0 EndX=-69 EndY=16 EndZ=0
    g25: Circle CenterX=-22 CenterY=20.125 CenterZ=0 NormalX=0 NormalY=0 NormalZ=1 AngleXU=0 Radius=4.125
  constraints (69):
    c: PointOnObject(g0,g-1)
    c: PointOnObject(g0,g-1)
    c: Coincident(g0,g1)
    c: Vertical(g1)
    c: Coincident(g1,g2)
    c: Horizontal(g2)
    c: Coincident(g2,g3)
    c: Coincident(g3,g0)
    c: Vertical(g3)
    c: PointOnObject(g4,g-1)
    c: Coincident(g4,g5)
    c: Vertical(g5)
    c: Coincident(g5,g6)
    c: Horizontal(g6)
    c: Symmetric(g4,g0,g-2)
    c: DistanceX(g2,g2) = 4
    c: Coincident(g7,g4)
    c: Coincident(g7,g0)
    c: DistanceX(g7,g7) = 40
    c: Equal(g6,g0)
    c: Horizontal(g9)
    c: Coincident(g9,g10)
    c: Coincident(g10,g8)
    c: Tangent(g10,g5)
    c: Tangent(g8,g2)
    c: Coincident(g11,g9)
    c: Coincident(g11,g5)
    c: Coincident(g12,g8)
    c: Coincident(g12,g1)
    c: DistanceY(g11,g11) = 64
    c: DistanceY(g5,g5) = 16
    c: Equal(g6,g4)
    c: Coincident(g13,g8)
    c: Coincident(g14,g13)
    c: Vertical(g14)
    c: Angle(g14,g13) = 2.35619
    c: Coincident(g14,g15)
    c: Horizontal(g15)
    c: Coincident(g15,g16)
    c: Vertical(g16)
    c: Coincident(g16,g17)
    c: Coincident(g17,g9)
    c: Parallel(g17,g13)
    c: DistanceX(g15,g15) = 4
    c: DistanceX(g15,g6) = 45
    c: Distance(g16,g13) = 4
    c: Coincident(g18,g6)
    c: Coincident(g18,g4)
    c: Coincident(g14,g19)
    c: Coincident(g15,g20)
    c: Coincident(g20,g19)
    c: Equal(g20,g19)
    c: Coincident(g6,g21)
    c: Coincident(g21,g22)
    c: Coincident(g23,g22)
    c: Coincident(g23,g6)
    c: Horizontal(g23)
    c: Coincident(g24,g22)
    c: Coincident(g24,g15)
    c: Horizontal(g24)
    c: Equal(g21,g22)
    c: Equal(g22,g20)
    c: Angle(g23,g22) = 0.523599
    c: Parallel(g22,g19)
    c: DistanceX(g25,g5) = 2
    c: DistanceY(g6,g25) = 4.125
    c: Diameter(g25) = 8.25
    c: DistanceY(g10,g10) = 4
    c: DistanceX(g9,g9) = 4
FEATURE [Part::Extrusion] Extrude013
  Base = -> Sketch011
  Dir = (0,-1,2e-16)
  DirMode = 2
  FaceMakerClass = Part::FaceMakerBullseye
  FaceMakerMode = 3
  LengthFwd = 4
  LengthRev = 0
  Placement = pos=(0,24,0) rot=(0,0,1;0rad)
  Solid = true
  Symmetric = false
  expr: LengthFwd = <<Variables>>.WallWidth
FEATURE [Part::MultiFuse] Fusion005  label="Stage 3 Paths"
  Shapes = -> [Extrude004,Extrude007]
FEATURE [Sketcher::SketchObject] Sketch012
  ArcFitTolerance = 1e-06
  FullyConstrained = true
  MakeInternals = false
  MapMode = 5
  Placement = pos=(0,0,0) rot=(1,0,0;1.5708rad)
  expr: Constraints[17] = <<Variables>>.ConnectorAngle
  expr: Constraints[2] = <<Variables>>.WallWidth
  expr: Constraints[4] = <<Variables>>.BinWidth
  sketch-geometry (7):
    g0: LineSegment StartX=-20 StartY=1e-16 StartZ=0 EndX=-24 EndY=0 EndZ=0
    g1: LineSegment [constr] StartX=-20 StartY=1e-16 StartZ=0 EndX=20 EndY=0 EndZ=0
    g2: LineSegment StartX=-24 StartY=0 StartZ=0 EndX=-22 EndY=1.1547 EndZ=0
    g3: LineSegment StartX=-22 StartY=1.1547 StartZ=0 EndX=-20 EndY=1e-16 EndZ=0
    g4: LineSegment StartX=20 StartY=0 StartZ=0 EndX=22 EndY=1.1547 EndZ=0
    g5: LineSegment StartX=22 StartY=1.1547 StartZ=0 EndX=24 EndY=-1e-16 EndZ=0
    g6: LineSegment StartX=24 StartY=-1e-16 StartZ=0 EndX=20 EndY=0 EndZ=0
  constraints (19):
    c: PointOnObject(g0,g-1)
    c: PointOnObject(g0,g-1)
    c: DistanceX(g0,g0) = 4
    c: Symmetric(g0,g1,g-2)
    c: DistanceX(g1,g1) = 40
    c: Coincident(g2,g3)
    c: Coincident(g3,g0)
    c: Coincident(g2,g0)
    c: Equal(g3,g2)
    c: Coincident(g1,g0)
    c: Coincident(g1,g4)
    c: Coincident(g4,g5)
    c: PointOnObject(g5,g-1)
    c: Coincident(g5,g6)
    c: Coincident(g6,g4)
    c: Equal(g4,g5)
    c: Equal(g6,g0)
    c: Angle(g0,g2) = 0.523599
    c: Parallel(g2,g4)
FEATURE [Part::Extrusion] Extrude014
  Base = -> Sketch012
  Dir = (0,-1,2e-16)
  DirMode = 2
  FaceMakerClass = Part::FaceMakerBullseye
  FaceMakerMode = 3
  LengthFwd = 200
  LengthRev = 0
  Placement = pos=(1,0,-20) rot=(0,0,1;0rad)
  Solid = true
  Symmetric = true
  expr: .Placement.Base.x = <<Variables>>.WallWidth / 4
  expr: .Placement.Base.z = <<Variables>>.WallWidth * -5
FEATURE [Part::MultiFuse] Fusion006
  Placement = pos=(-1,0,0) rot=(0,0,1;0rad)
  Shapes = -> [Extrude011,Extrude010]
FEATURE [Part::Cut] Cut  label="Stage 1 Paths"
  Base = -> Fusion006
  Tool = -> Extrude014
FEATURE [Sketcher::SketchObject] Sketch013
  ArcFitTolerance = 1e-06
  FullyConstrained = true
  MakeInternals = false
  Placement = pos=(0,0,0) rot=(0.57735,0.57735,0.57735;2.0944rad)
  expr: Constraints[10] = <<Variables>>.ConnectorAngle
  expr: Constraints[8] = <<Variables>>.WallWidth
  expr: Constraints[9] = <<Variables>>.BinWidth / 2
  sketch-geometry (4):
    g0: LineSegment StartX=-24 StartY=0 StartZ=0 EndX=-22 EndY=1.1547 EndZ=0
    g1: LineSegment StartX=-22 StartY=1.1547 StartZ=0 EndX=-20 EndY=0 EndZ=0
    g2: LineSegment StartX=-20 StartY=0 StartZ=0 EndX=-24 EndY=0 EndZ=0
    g3: LineSegment [constr] StartX=-20 StartY=0 StartZ=0 EndX=0 EndY=0 EndZ=0
  constraints (11):
    c: PointOnObject(g0,g-1)
    c: Coincident(g0,g1)
    c: PointOnObject(g1,g-1)
    c: Coincident(g1,g2)
    c: Coincident(g2,g0)
    c: Coincident(g1,g3)
    c: Coincident(g3,g-1)
    c: Equal(g0,g1)
    c: DistanceX(g2,g2) = 4
    c: DistanceX(g3,g3) = 20
    c: Angle(g2,g0) = 0.523599
FEATURE [Part::Extrusion] Extrude015
  Base = -> Sketch013
  Dir = (1,0,0)
  DirMode = 2
  FaceMakerClass = Part::FaceMakerBullseye
  FaceMakerMode = 3
  LengthFwd = 50
  LengthRev = 0
  Placement = pos=(0,44,0) rot=(0,0,1;0rad)
  Solid = true
  Symmetric = true
  expr: .Placement.Base.y = <<Extrude013>>.Placement.Base.y + <<Variables>>.BinWidth / 2
FEATURE [Part::Extrusion] Extrude012
  Base = -> Sketch010
  Dir = (0,-1,2e-16)
  DirMode = 2
  FaceMakerClass = Part::FaceMakerBullseye
  FaceMakerMode = 3
  LengthFwd = 44
  LengthRev = 0
  Placement = pos=(0,-2,0) rot=(0,0,1;0rad)
  Solid = true
  Symmetric = true
  expr: .Placement.Base.y = <<Variables>>.WallWidth / -2
  expr: LengthFwd = <<Variables>>.BinWidth + <<Variables>>.WallWidth
FEATURE [Part::Cut] Cut001
  Base = -> Extrude013
  Tool = -> Extrude015
FEATURE [Part::MultiFuse] Fusion004  label="Reject Path"
  Shapes = -> [Extrude012,Cut001]
FEATURE [Sketcher::SketchObject] Sketch014
  ArcFitTolerance = 1e-06
  FullyConstrained = true
  MakeInternals = false
  MapMode = 5
  expr: Constraints[1] = <<Variables>>.FlapPinDiameter
  sketch-geometry (1):
    g0: Circle CenterX=0 CenterY=0 CenterZ=0 NormalX=0 NormalY=0 NormalZ=1 AngleXU=0 Radius=4
  constraints (2):
    c: Coincident(g0,g-1)
    c: Diameter(g0) = 8
FEATURE [Part::Extrusion] Extrude016
  Base = -> Sketch014
  Dir = (0,0,1)
  DirMode = 2
  FaceMakerClass = Part::FaceMakerBullseye
  FaceMakerMode = 3
  LengthFwd = 45
  LengthRev = 0
  Solid = true
  Symmetric = false
  expr: LengthFwd = <<Variables>>.BinWidth + <<Variables>>.WallWidth + <<Variables>>.Tolerance
FEATURE [Sketcher::SketchObject] Sketch015
  ArcFitTolerance = 1e-06
  AttachmentSupport = -> [Extrude016]
  FullyConstrained = true
  MakeInternals = false
  MapMode = 3
  Placement = pos=(0,0,0) rot=(1,0,0;1.5708rad)
  expr: Constraints[10] = <<Variables>>.BinWidth
  expr: Constraints[11] = <<Variables>>.WallWidth
  expr: Constraints[8] = <<Variables>>.BinWidth
  sketch-geometry (4):
    g0: LineSegment StartX=0 StartY=44 StartZ=0 EndX=-40 EndY=44 EndZ=0
    g1: LineSegment StartX=-40 StartY=44 StartZ=0 EndX=-40 EndY=4 EndZ=0
    g2: LineSegment StartX=-40 StartY=4 StartZ=0 EndX=0 EndY=4 EndZ=0
    g3: LineSegment StartX=0 StartY=4 StartZ=0 EndX=0 EndY=44 EndZ=0
  constraints (12):
    c: Coincident(g0,g1)
    c: Coincident(g1,g2)
    c: Coincident(g2,g3)
    c: Coincident(g3,g0)
    c: Horizontal(g0)
    c: Horizontal(g2)
    c: Vertical(g1)
    c: Vertical(g3)
    c: DistanceX(g0,g0) = 40
    c: PointOnObject(g0,g-2)
    c: DistanceY(g1,g1) = 40
    c: Distance(g1,g-1) = 4
FEATURE [Part::Extrusion] Extrude017
  Base = -> Sketch015
  Dir = (0,-1,2e-16)
  DirMode = 2
  FaceMakerClass = Part::FaceMakerBullseye
  FaceMakerMode = 3
  LengthFwd = 4
  LengthRev = 0
  Solid = true
  Symmetric = true
  expr: LengthFwd = <<Variables>>.WallWidth
FEATURE [Part::Chamfer] Chamfer
  Base = -> Extrude017
  EdgeLinks = -> Extrude017 [Edge6,Edge7]
  Edges = 2 edges r=1.5: [Edge6,Edge7]
FEATURE [Sketcher::SketchObject] Sketch016
  ArcFitTolerance = 1e-06
  FullyConstrained = true
  MakeInternals = false
  MapMode = 5
  expr: Constraints[1] = <<Variables>>.FlapPinDiameter
  sketch-geometry (1):
    g0: Circle CenterX=0 CenterY=0 CenterZ=0 NormalX=0 NormalY=0 NormalZ=1 AngleXU=0 Radius=4
  constraints (2):
    c: Coincident(g0,g-1)
    c: Diameter(g0) = 8
FEATURE [Part::Extrusion] Extrude020
  Base = -> Sketch016
  Dir = (0,0,1)
  DirMode = 2
  FaceMakerClass = Part::FaceMakerBullseye
  FaceMakerMode = 3
  LengthFwd = 49
  LengthRev = 0
  Solid = true
  Symmetric = false
  expr: LengthFwd = <<Variables>>.BinWidth + <<Variables>>.WallWidth * 2 + <<Variables>>.Tolerance
FEATURE [Sketcher::SketchObject] Sketch017
  ArcFitTolerance = 1e-06
  AttachmentSupport = -> [Extrude020]
  FullyConstrained = true
  MakeInternals = false
  MapMode = 3
  Placement = pos=(0,0,0) rot=(1,0,0;1.5708rad)
  expr: Constraints[10] = <<Variables>>.BinWidth + <<Variables>>.WallWidth
  expr: Constraints[11] = <<Variables>>.WallWidth
  expr: Constraints[8] = <<Variables>>.BinHeight
  sketch-geometry (4):
    g0: LineSegment StartX=0 StartY=48 StartZ=0 EndX=-60 EndY=48 EndZ=0
    g1: LineSegment StartX=-60 StartY=48 StartZ=0 EndX=-60 EndY=4 EndZ=0
    g2: LineSegment StartX=-60 StartY=4 StartZ=0 EndX=0 EndY=4 EndZ=0
    g3: LineSegment StartX=0 StartY=4 StartZ=0 EndX=0 EndY=48 EndZ=0
  constraints (12):
    c: Coincident(g0,g1)
    c: Coincident(g1,g2)
    c: Coincident(g2,g3)
    c: Coincident(g3,g0)
    c: Horizontal(g0)
    c: Horizontal(g2)
    c: Vertical(g1)
    c: Vertical(g3)
    c: DistanceX(g0,g0) = 60
    c: PointOnObject(g0,g-2)
    c: DistanceY(g1,g1) = 44
    c: Distance(g1,g-1) = 4
FEATURE [Part::Extrusion] Extrude021
  Base = -> Sketch017
  Dir = (0,-1,2e-16)
  DirMode = 2
  FaceMakerClass = Part::FaceMakerBullseye
  FaceMakerMode = 3
  LengthFwd = 4
  LengthRev = 0
  Solid = true
  Symmetric = true
  expr: LengthFwd = <<Variables>>.WallWidth
FEATURE [Part::Chamfer] Chamfer001
  Base = -> Extrude021
  EdgeLinks = -> Extrude021 [Edge6,Edge7]
  Edges = 2 edges r=1.5: [Edge6,Edge7]
FEATURE [App::Link] Reject_Flap  label="Reject Flap001"
  LinkPlacement = pos=(-22,24,260) rot=(0.57735,0.57735,-0.57735;2.0944rad)
  LinkedObject = -> Fusion008
  Placement = pos=(-22,24,260) rot=(0.57735,0.57735,-0.57735;2.0944rad)
FEATURE [App::Link] Reject_Path  label="Reject Path001"
  LinkPlacement = pos=(-1.90735e-06,9.83477e-07,240) rot=(0,0,1;0rad)
  LinkedObject = -> Fusion004
  Placement = pos=(-1.90735e-06,9.83477e-07,240) rot=(0,0,1;0rad)
FEATURE [App::Link] Stage_1_Paths  label="Stage 1 Paths001"
  LinkPlacement = pos=(-1,0,192) rot=(0,0,1;0rad)
  LinkedObject = -> Cut
  Placement = pos=(-1,0,192) rot=(0,0,1;0rad)
FEATURE [App::Link] Stage_3_Paths  label="Stage 3 Paths001"
  LinkPlacement = pos=(-98,-8,0) rot=(0,0,1;0rad)
  LinkedObject = -> Fusion005
  Placement = pos=(-98,-8,0) rot=(0,0,1;0rad)
FEATURE [App::Link] Stage_2_Paths  label="Stage 2 Paths001"
  LinkPlacement = pos=(0,-8,74) rot=(0,0,1;0rad)
  LinkedObject = -> Fusion002
  Placement = pos=(0,-8,74) rot=(0,0,1;0rad)
FEATURE [App::Link] Stage_2_Paths001  label="Stage 2 Paths002"
  LinkPlacement = pos=(0,8,74) rot=(0,0,1;3.14159rad)
  LinkedObject = -> Fusion002
  Placement = pos=(0,8,74) rot=(0,0,1;3.14159rad)
FEATURE [App::Link] Stage_3_Paths001  label="Stage 3 Paths002"
  LinkPlacement = pos=(98,-8,0) rot=(0,0,1;0rad)
  LinkedObject = -> Fusion005
  Placement = pos=(98,-8,0) rot=(0,0,1;0rad)
FEATURE [App::Link] Stage_3_Paths002  label="Stage 3 Paths003"
  LinkPlacement = pos=(-98,8,1.90735e-06) rot=(0,0,1;3.14159rad)
  LinkedObject = -> Fusion005
  Placement = pos=(-98,8,1.90735e-06) rot=(0,0,1;3.14159rad)
FEATURE [App::Link] Stage_3_Paths003  label="Stage 3 Paths004"
  LinkPlacement = pos=(98,8,3.6e-15) rot=(0,0,1;3.14159rad)
  LinkedObject = -> Fusion005
  Placement = pos=(98,8,3.6e-15) rot=(0,0,1;3.14159rad)
FEATURE [App::Link] Flap  label="Flap001"
  LinkPlacement = pos=(-147,-8,4) rot=(0.615789,0.615789,-0.615789;2.0944rad)
  LinkedObject = -> Fusion007
  Placement = pos=(-147,-8,4) rot=(0.615789,0.615789,-0.615789;2.0944rad)
FEATURE [App::Link] Flap001  label="Flap002"
  LinkPlacement = pos=(-48.9998,-8,4) rot=(0.615789,0.615789,-0.615789;2.0944rad)
  LinkedObject = -> Fusion007
  Placement = pos=(-48.9998,-8,4) rot=(0.615789,0.615789,-0.615789;2.0944rad)
FEATURE [App::Link] Flap002  label="Flap003"
  LinkPlacement = pos=(49.0008,-8,4) rot=(0.615789,0.615789,-0.615789;2.0944rad)
  LinkedObject = -> Fusion007
  Placement = pos=(49.0008,-8,4) rot=(0.615789,0.615789,-0.615789;2.0944rad)
FEATURE [App::Link] Flap003  label="Flap004"
  LinkPlacement = pos=(147.001,-8,4.00001) rot=(0.615789,0.615789,-0.615789;2.0944rad)
  LinkedObject = -> Fusion007
  Placement = pos=(147.001,-8,4.00001) rot=(0.615789,0.615789,-0.615789;2.0944rad)
FEATURE [App::Link] Bin_Holder  label="Bin Holder001"
  LinkPlacement = pos=(-171.5,-12,-110) rot=(0,0,1;0rad)
  LinkedObject = -> Fillet001
  Placement = pos=(-171.5,-12,-110) rot=(0,0,1;0rad)
FEATURE [App::Link] Bin_Holder001  label="Bin Holder002"
  LinkPlacement = pos=(-122.5,-12,-110) rot=(0,0,1;0rad)
  LinkedObject = -> Fillet001
  Placement = pos=(-122.5,-12,-110) rot=(0,0,1;0rad)
FEATURE [App::Link] Bin_Holder002  label="Bin Holder003"
  LinkPlacement = pos=(-73.5,-12,-110) rot=(0,0,1;0rad)
  LinkedObject = -> Fillet001
  Placement = pos=(-73.5,-12,-110) rot=(0,0,1;0rad)
FEATURE [App::Link] Bin_Holder003  label="Bin Holder004"
  LinkPlacement = pos=(-24.5,-12,-110) rot=(0,0,1;0rad)
  LinkedObject = -> Fillet001
  Placement = pos=(-24.5,-12,-110) rot=(0,0,1;0rad)
FEATURE [App::Link] Bin_Holder004  label="Bin Holder005"
  LinkPlacement = pos=(24.5,-12,-110) rot=(0,0,1;0rad)
  LinkedObject = -> Fillet001
  Placement = pos=(24.5,-12,-110) rot=(0,0,1;0rad)
FEATURE [App::Link] Bin_Holder005  label="Bin Holder006"
  LinkPlacement = pos=(73.5,-12,-110) rot=(0,0,1;0rad)
  LinkedObject = -> Fillet001
  Placement = pos=(73.5,-12,-110) rot=(0,0,1;0rad)
FEATURE [App::Link] Bin_Holder006  label="Bin Holder007"
  LinkPlacement = pos=(122.5,-12,-110) rot=(0,0,1;0rad)
  LinkedObject = -> Fillet001
  Placement = pos=(122.5,-12,-110) rot=(0,0,1;0rad)
FEATURE [App::Link] Bin_Holder007  label="Bin Holder008"
  LinkPlacement = pos=(171.481,-12,-110.154) rot=(0,0,1;0rad)
  LinkedObject = -> Fillet001
  Placement = pos=(171.481,-12,-110.154) rot=(0,0,1;0rad)
FEATURE [App::Link] Bin_Holder008  label="Bin Holder009"
  LinkPlacement = pos=(171.5,12,-110) rot=(0,0,1;3.14159rad)
  LinkedObject = -> Fillet001
  Placement = pos=(171.5,12,-110) rot=(0,0,1;3.14159rad)
FEATURE [App::Link] Bin_Holder009  label="Bin Holder010"
  LinkPlacement = pos=(122.5,12,-110) rot=(0,0,1;3.14159rad)
  LinkedObject = -> Fillet001
  Placement = pos=(122.5,12,-110) rot=(0,0,1;3.14159rad)
FEATURE [App::Link] Bin_Holder010  label="Bin Holder011"
  LinkPlacement = pos=(73.5,12,-110) rot=(0,0,1;3.14159rad)
  LinkedObject = -> Fillet001
  Placement = pos=(73.5,12,-110) rot=(0,0,1;3.14159rad)
FEATURE [App::Link] Bin_Holder011  label="Bin Holder012"
  LinkPlacement = pos=(24.5,12,-110) rot=(0,0,1;3.14159rad)
  LinkedObject = -> Fillet001
  Placement = pos=(24.5,12,-110) rot=(0,0,1;3.14159rad)
FEATURE [App::Link] Bin_Holder012  label="Bin Holder013"
  LinkPlacement = pos=(-24.5,12,-110) rot=(0,0,1;3.14159rad)
  LinkedObject = -> Fillet001
  Placement = pos=(-24.5,12,-110) rot=(0,0,1;3.14159rad)
FEATURE [App::Link] Bin_Holder013  label="Bin Holder014"
  LinkPlacement = pos=(-73.5,12,-110) rot=(0,0,1;3.14159rad)
  LinkedObject = -> Fillet001
  Placement = pos=(-73.5,12,-110) rot=(0,0,1;3.14159rad)
FEATURE [App::Link] Bin_Holder014  label="Bin Holder015"
  LinkPlacement = pos=(-122.5,12,-110) rot=(0,0,1;3.14159rad)
  LinkedObject = -> Fillet001
  Placement = pos=(-122.5,12,-110) rot=(0,0,1;3.14159rad)
FEATURE [App::Link] Bin_Holder015  label="Bin Holder016"
  LinkPlacement = pos=(-171.5,12,-110) rot=(0,0,1;3.14159rad)
  LinkedObject = -> Fillet001
  Placement = pos=(-171.5,12,-110) rot=(0,0,1;3.14159rad)
FEATURE [App::Link] Bin_Holder016  label="Bin Holder017"
  LinkPlacement = pos=(-48.5,20,176) rot=(0,0,1;0rad)
  LinkedObject = -> Fillet001
  Placement = pos=(-48.5,20,176) rot=(0,0,1;0rad)
FEATURE [App::Link] Bin  label="Bin001"
  LinkPlacement = pos=(-171.5,-30,-106) rot=(0,0,1;0rad)
  LinkedObject = -> Fillet
  Placement = pos=(-171.5,-30,-106) rot=(0,0,1;0rad)
FEATURE [App::Link] Bin001  label="Bin002"
  LinkPlacement = pos=(-122.5,-30,-106) rot=(0,0,1;0rad)
  LinkedObject = -> Fillet
  Placement = pos=(-122.5,-30,-106) rot=(0,0,1;0rad)
FEATURE [App::Link] Bin002  label="Bin003"
  LinkPlacement = pos=(-73.5,-30,-106) rot=(0,0,1;0rad)
  LinkedObject = -> Fillet
  Placement = pos=(-73.5,-30,-106) rot=(0,0,1;0rad)
FEATURE [App::Link] Bin003  label="Bin004"
  LinkPlacement = pos=(-24.5,-30,-106) rot=(0,0,1;0rad)
  LinkedObject = -> Fillet
  Placement = pos=(-24.5,-30,-106) rot=(0,0,1;0rad)
FEATURE [App::Link] Bin004  label="Bin005"
  LinkPlacement = pos=(24.5,-30,-106) rot=(0,0,1;0rad)
  LinkedObject = -> Fillet
  Placement = pos=(24.5,-30,-106) rot=(0,0,1;0rad)
FEATURE [App::Link] Bin005  label="Bin006"
  LinkPlacement = pos=(73.5,-30,-106) rot=(0,0,1;0rad)
  LinkedObject = -> Fillet
  Placement = pos=(73.5,-30,-106) rot=(0,0,1;0rad)
FEATURE [App::Link] Bin006  label="Bin007"
  LinkPlacement = pos=(122.5,-30,-106) rot=(0,0,1;0rad)
  LinkedObject = -> Fillet
  Placement = pos=(122.5,-30,-106) rot=(0,0,1;0rad)
FEATURE [App::Link] Bin007  label="Bin008"
  LinkPlacement = pos=(171.5,-30,-106) rot=(0,0,1;0rad)
  LinkedObject = -> Fillet
  Placement = pos=(171.5,-30,-106) rot=(0,0,1;0rad)
FEATURE [App::Link] Bin008  label="Bin009"
  LinkPlacement = pos=(171.5,30,-106) rot=(0,0,1;0rad)
  LinkedObject = -> Fillet
  Placement = pos=(171.5,30,-106) rot=(0,0,1;0rad)
FEATURE [App::Link] Bin009  label="Bin010"
  LinkPlacement = pos=(122.5,30,-106) rot=(0,0,1;0rad)
  LinkedObject = -> Fillet
  Placement = pos=(122.5,30,-106) rot=(0,0,1;0rad)
FEATURE [App::Link] Bin010  label="Bin011"
  LinkPlacement = pos=(73.5,30,-106) rot=(0,0,1;0rad)
  LinkedObject = -> Fillet
  Placement = pos=(73.5,30,-106) rot=(0,0,1;0rad)
FEATURE [App::Link] Bin011  label="Bin012"
  LinkPlacement = pos=(24.5,30,-106) rot=(0,0,1;0rad)
  LinkedObject = -> Fillet
  Placement = pos=(24.5,30,-106) rot=(0,0,1;0rad)
FEATURE [App::Link] Bin012  label="Bin013"
  LinkPlacement = pos=(-24.5,30,-106) rot=(0,0,1;0rad)
  LinkedObject = -> Fillet
  Placement = pos=(-24.5,30,-106) rot=(0,0,1;0rad)
FEATURE [App::Link] Bin013  label="Bin014"
  LinkPlacement = pos=(-73.5,30,-106) rot=(0,0,1;0rad)
  LinkedObject = -> Fillet
  Placement = pos=(-73.5,30,-106) rot=(0,0,1;0rad)
FEATURE [App::Link] Bin014  label="Bin015"
  LinkPlacement = pos=(-122.5,30,-106) rot=(0,0,1;0rad)
  LinkedObject = -> Fillet
  Placement = pos=(-122.5,30,-106) rot=(0,0,1;0rad)
FEATURE [App::Link] Bin015  label="Bin016"
  LinkPlacement = pos=(-171.5,30,-106) rot=(0,0,1;0rad)
  LinkedObject = -> Fillet
  Placement = pos=(-171.5,30,-106) rot=(0,0,1;0rad)
FEATURE [App::Link] Bin016  label="Bin017"
  LinkPlacement = pos=(-48.5,-1.42753e-05,180) rot=(0,0,1;0rad)
  LinkedObject = -> Fillet
  Placement = pos=(-48.5,-1.42753e-05,180) rot=(0,0,1;0rad)
FEATURE [App::Link] Flap004  label="Flap005"
  LinkPlacement = pos=(147.001,8,4.00001) rot=(0.615789,-0.615789,-0.615789;4.18879rad)
  LinkedObject = -> Fusion007
  Placement = pos=(147.001,8,4.00001) rot=(0.615789,-0.615789,-0.615789;4.18879rad)
FEATURE [App::Link] Flap005  label="Flap006"
  LinkPlacement = pos=(49.0008,8,4) rot=(0.615789,-0.615789,-0.615789;4.18879rad)
  LinkedObject = -> Fusion007
  Placement = pos=(49.0008,8,4) rot=(0.615789,-0.615789,-0.615789;4.18879rad)
FEATURE [App::Link] Flap006  label="Flap007"
  LinkPlacement = pos=(-48.9998,8,4) rot=(0.615789,-0.615789,-0.615789;4.18879rad)
  LinkedObject = -> Fusion007
  Placement = pos=(-48.9998,8,4) rot=(0.615789,-0.615789,-0.615789;4.18879rad)
FEATURE [App::Link] Flap007  label="Flap008"
  LinkPlacement = pos=(-147,8,4) rot=(0.615789,-0.615789,-0.615789;4.18879rad)
  LinkedObject = -> Fusion007
  Placement = pos=(-147,8,4) rot=(0.615789,-0.615789,-0.615789;4.18879rad)
FEATURE [App::Link] Flap008  label="Flap009"
  LinkPlacement = pos=(0.000612859,-8,152) rot=(0.57735,0.57735,-0.57735;2.0944rad)
  LinkedObject = -> Fusion007
  Placement = pos=(0.000612859,-8,152) rot=(0.57735,0.57735,-0.57735;2.0944rad)
FEATURE [App::Link] Flap009  label="Flap010"
  LinkPlacement = pos=(0.000616115,8,152) rot=(-0.57735,0.57735,0.57735;2.0944rad)
  LinkedObject = -> Fusion007
  Placement = pos=(0.000616115,8,152) rot=(-0.57735,0.57735,0.57735;2.0944rad)
FEATURE [App::Link] Flap010  label="Flap011"
  LinkPlacement = pos=(24,-0.000116557,196) rot=(-0.707107,0,0.707107;3.14159rad)
  LinkedObject = -> Fusion007
  Placement = pos=(24,-0.000116557,196) rot=(-0.707107,0,0.707107;3.14159rad)
FEATURE [Sketcher::SketchObject] Sketch018
  ArcFitTolerance = 1e-06
  FullyConstrained = true
  MakeInternals = false
  expr: Constraints[13] = <<Variables>>.WallWidth - <<Variables>>.Tolerance - 0.05 mm
  sketch-geometry (6):
    g0: LineSegment StartX=-1.475 StartY=2.55477 StartZ=0 EndX=1.475 EndY=2.55477 EndZ=0
    g1: LineSegment StartX=1.475 StartY=2.55477 StartZ=0 EndX=2.95 EndY=-5e-16 EndZ=0
    g2: LineSegment StartX=2.95 StartY=-5e-16 StartZ=0 EndX=1.475 EndY=-2.55477 EndZ=0
    g3: LineSegment StartX=1.475 StartY=-2.55477 StartZ=0 EndX=-1.475 EndY=-2.55477 EndZ=0
    g4: LineSegment StartX=-1.475 StartY=-2.55477 StartZ=0 EndX=-2.95 EndY=4e-16 EndZ=0
    g5: LineSegment StartX=-2.95 StartY=4e-16 StartZ=0 EndX=-1.475 EndY=2.55477 EndZ=0
  constraints (15):
    c: Coincident(g0,g1)
    c: PointOnObject(g1,g-1)
    c: Coincident(g1,g2)
    c: Coincident(g2,g3)
    c: Coincident(g3,g4)
    c: PointOnObject(g4,g-1)
    c: Coincident(g4,g5)
    c: Coincident(g5,g0)
    c: Symmetric(g0,g0,g-2)
    c: Symmetric(g0,g3,g-1)
    c: Symmetric(g2,g3,g-2)
    c: Equal(g4,g3)
    c: Equal(g2,g3)
    c: DistanceX(g0,g0) = 2.95
    c: Angle(g0,g1) = 2.0944
FEATURE [Part::Extrusion] Extrude023
  Base = -> Sketch018
  Dir = (0,0,1)
  DirMode = 2
  FaceMakerClass = Part::FaceMakerBullseye
  FaceMakerMode = 3
  LengthFwd = 0
  LengthRev = 7
  Solid = true
  Symmetric = false
  expr: LengthRev = <<Variables>>.WallWidth * 2 - 1 mm
FEATURE [Part::MultiFuse] Fusion007  label="Flap"
  Placement = pos=(0,0,0) rot=(0,1,0;3.14159rad)
  Shapes = -> [Extrude016,Chamfer,Extrude023]
FEATURE [Sketcher::SketchObject] Sketch019
  ArcFitTolerance = 1e-06
  FullyConstrained = true
  MakeInternals = false
  expr: Constraints[13] = <<Variables>>.WallWidth - 1 mm
  sketch-geometry (6):
    g0: LineSegment StartX=-1.5 StartY=2.59808 StartZ=0 EndX=1.5 EndY=2.59808 EndZ=0
    g1: LineSegment StartX=1.5 StartY=2.59808 StartZ=0 EndX=3 EndY=-2e-16 EndZ=0
    g2: LineSegment StartX=3 StartY=-2e-16 StartZ=0 EndX=1.5 EndY=-2.59808 EndZ=0
    g3: LineSegment StartX=1.5 StartY=-2.59808 StartZ=0 EndX=-1.5 EndY=-2.59808 EndZ=0
    g4: LineSegment StartX=-1.5 StartY=-2.59808 StartZ=0 EndX=-3 EndY=2e-16 EndZ=0
    g5: LineSegment StartX=-3 StartY=2e-16 StartZ=0 EndX=-1.5 EndY=2.59808 EndZ=0
  constraints (15):
    c: Coincident(g0,g1)
    c: PointOnObject(g1,g-1)
    c: Coincident(g1,g2)
    c: Coincident(g2,g3)
    c: Coincident(g3,g4)
    c: PointOnObject(g4,g-1)
    c: Coincident(g4,g5)
    c: Coincident(g5,g0)
    c: Symmetric(g0,g0,g-2)
    c: Symmetric(g0,g3,g-1)
    c: Symmetric(g2,g3,g-2)
    c: Equal(g4,g3)
    c: Equal(g2,g3)
    c: DistanceX(g0,g0) = 3
    c: Angle(g0,g1) = 2.0944
FEATURE [Part::Extrusion] Extrude024
  Base = -> Sketch019
  Dir = (0,0,1)
  DirMode = 2
  FaceMakerClass = Part::FaceMakerBullseye
  FaceMakerMode = 3
  LengthFwd = 0
  LengthRev = 8
  Solid = true
  Symmetric = false
  expr: LengthRev = <<Variables>>.WallWidth * 2
FEATURE [Part::MultiFuse] Fusion008  label="Reject Flap"
  Placement = pos=(0,0,0) rot=(0,1,0;3.14159rad)
  Shapes = -> [Extrude020,Chamfer001,Extrude024]
FEATURE [Sketcher::SketchObject] Sketch021
  ArcFitTolerance = 1e-06
  FullyConstrained = true
  MakeInternals = false
  expr: Constraints[13] = <<Variables>>.WallWidth - 1 mm
  sketch-geometry (6):
    g0: LineSegment StartX=-1.5 StartY=2.59808 StartZ=0 EndX=1.5 EndY=2.59808 EndZ=0
    g1: LineSegment StartX=1.5 StartY=2.59808 StartZ=0 EndX=3 EndY=-2e-16 EndZ=0
    g2: LineSegment StartX=3 StartY=-2e-16 StartZ=0 EndX=1.5 EndY=-2.59808 EndZ=0
    g3: LineSegment StartX=1.5 StartY=-2.59808 StartZ=0 EndX=-1.5 EndY=-2.59808 EndZ=0
    g4: LineSegment StartX=-1.5 StartY=-2.59808 StartZ=0 EndX=-3 EndY=2e-16 EndZ=0
    g5: LineSegment StartX=-3 StartY=2e-16 StartZ=0 EndX=-1.5 EndY=2.59808 EndZ=0
  constraints (15):
    c: Coincident(g0,g1)
    c: PointOnObject(g1,g-1)
    c: Coincident(g1,g2)
    c: Coincident(g2,g3)
    c: Coincident(g3,g4)
    c: PointOnObject(g4,g-1)
    c: Coincident(g4,g5)
    c: Coincident(g5,g0)
    c: Symmetric(g0,g0,g-2)
    c: Symmetric(g0,g3,g-1)
    c: Symmetric(g2,g3,g-2)
    c: Equal(g4,g3)
    c: Equal(g2,g3)
    c: DistanceX(g0,g0) = 3
    c: Angle(g0,g1) = 2.0944
FEATURE [Part::Extrusion] Extrude025
  Base = -> Sketch021
  Dir = (0,0,1)
  DirMode = 2
  FaceMakerClass = Part::FaceMakerBullseye
  FaceMakerMode = 3
  LengthFwd = 16
  LengthRev = 0
  Solid = true
  Symmetric = true
  expr: LengthFwd = <<Variables>>.WallWidth * 4
FEATURE [Part::Part2DObjectPython] InvoluteGear  # Draft 2D object (typed FeaturePython)
  AddendumCoefficient = 1
  DedendumCoefficient = 1
  ExternalGear = true
  HighPrecision = true
  Modules = 1
  NumberOfTeeth = 10
  PressureAngle = 20
  ProfileShiftCoefficient = 0
  RootFilletCoefficient = 0.38
FEATURE [Part::Extrusion] Extrude026
  Base = -> InvoluteGear
  Dir = (0,0,1)
  DirMode = 2
  FaceMakerClass = Part::FaceMakerBullseye
  FaceMakerMode = 3
  LengthFwd = 16
  LengthRev = 0
  Solid = true
  Symmetric = true
  expr: LengthFwd = <<Variables>>.WallWidth * 4
FEATURE [Part::Cut] Cut002  label="Flap Connector"
  Base = -> Extrude026
  Tool = -> Extrude025
FEATURE [App::FeaturePython] GroundedJoint  # Assembly grounded joint (typed FeaturePython)
  ObjectToGround = -> Bin_Holder
  Placement = pos=(-171.5,-12,-110) rot=(0,0,1;0rad)
FEATURE [Assembly::JointGroup] Joints
  Group = -> [GroundedJoint]
FEATURE [App::Link] Flap011  label="Flap012"
  LinkPlacement = pos=(-98,-8,41) rot=(0.57735,0.57735,-0.57735;2.0944rad)
  LinkedObject = -> Fusion007
  Placement = pos=(-98,-8,41) rot=(0.57735,0.57735,-0.57735;2.0944rad)
FEATURE [App::Link] Flap012  label="Flap013"
  LinkPlacement = pos=(-98,8,41) rot=(-0.57735,0.57735,0.57735;2.0944rad)
  LinkedObject = -> Fusion007
  Placement = pos=(-98,8,41) rot=(-0.57735,0.57735,0.57735;2.0944rad)
FEATURE [App::Link] Flap013  label="Flap014"
  LinkPlacement = pos=(98,-8,41) rot=(0.57735,0.57735,-0.57735;2.0944rad)
  LinkedObject = -> Fusion007
  Placement = pos=(98,-8,41) rot=(0.57735,0.57735,-0.57735;2.0944rad)
FEATURE [App::Link] Flap014  label="Flap015"
  LinkPlacement = pos=(98,8,41) rot=(-0.57735,0.57735,0.57735;2.0944rad)
  LinkedObject = -> Fusion007
  Placement = pos=(98,8,41) rot=(-0.57735,0.57735,0.57735;2.0944rad)
FEATURE [Assembly::AssemblyObject] Assembly
  Group = -> [Joints,Reject_Path,Stage_1_Paths,Stage_2_Paths,Stage_2_Paths001,Stage_3_Paths,Stage_3_Paths001,Stage_3_Paths002,Stage_3_Paths003,Bin_Holder,Bin_Holder001,Bin_Holder002,Bin_Holder003,Bin_Holder004,Bin_Holder005,Bin_Holder006,Bin_Holder007,Bin_Holder008,Bin_Holder009,Bin_Holder010,Bin_Holder011,Bin_Holder012,Bin_Holder013,Bin_Holder014,Bin_Holder015,Bin_Holder016,Bin,Bin001,Bin002,Bin003,Bin004,+29 more]
  Origin = -> Origin
  Type = Assembly
FEATURE [Sketcher::SketchObject] Sketch023
  ArcFitTolerance = 1e-06
  FullyConstrained = true
  MakeInternals = false
  Placement = pos=(0,0,0) rot=(0.57735,0.57735,0.57735;2.0944rad)
  expr: Constraints[0] = <<Variables>>.FlapPinDiameter + <<Variables>>.FlapTolerance
  expr: Constraints[1] = <<Variables>>.BinWidth * 1.5 - (<<Variables>>.FlapPinDiameter / 2 + <<Variables>>.FlapTolerance)
  expr: Constraints[2] = <<Variables>>.BinWidth / 2 + <<Variables>>.WallWidth - (<<Variables>>.FlapPinDiameter / 2 + <<Variables>>.FlapTolerance)
  sketch-geometry (1):
    g0: Circle CenterX=-19.75 CenterY=55.75 CenterZ=0 NormalX=0 NormalY=0 NormalZ=1 AngleXU=0 Radius=4.125
  constraints (3):
    c: Diameter(g0) = 8.25
    c: Distance(g0,g-1) = 55.75
    c: Distance(g0,g-2) = 19.75
FEATURE [Part::Extrusion] Extrude028
  Base = -> Sketch023
  Dir = (1,0,0)
  DirMode = 2
  FaceMakerClass = Part::FaceMakerBullseye
  FaceMakerMode = 3
  LengthFwd = 60
  LengthRev = 0
  Placement = pos=(-21.5,0,0) rot=(0,0,1;0rad)
  Solid = true
  Symmetric = false
  expr: .Placement.Base.x = <<Variables>>.BinWidth / -2 - <<Variables>>.Tolerance * 1.5
  expr: LengthFwd = <<Variables>>.BinWidth * 1.5
FEATURE [Sketcher::SketchObject] Sketch022
  ArcFitTolerance = 1e-06
  FullyConstrained = true
  MakeInternals = false
  MapMode = 5
  Placement = pos=(0,0,0) rot=(1,0,0;1.5708rad)
  expr: Constraints[20] = <<Variables>>.WallWidth
  expr: Constraints[21] = <<Variables>>.BinWidth
  expr: Constraints[22] = <<Variables>>.BinWidth * 1.5 + <<Variables>>.WallWidth
  sketch-geometry (8):
    g0: LineSegment StartX=-24 StartY=0 StartZ=0 EndX=-20 EndY=0 EndZ=0
    g1: LineSegment StartX=-20 StartY=0 StartZ=0 EndX=-20 EndY=64 EndZ=0
    g2: LineSegment StartX=-20 StartY=64 StartZ=0 EndX=-24 EndY=64 EndZ=0
    g3: LineSegment StartX=-24 StartY=64 StartZ=0 EndX=-24 EndY=0 EndZ=0
    g4: LineSegment StartX=20 StartY=0 StartZ=0 EndX=24 EndY=0 EndZ=0
    g5: LineSegment StartX=24 StartY=0 StartZ=0 EndX=24 EndY=64 EndZ=0
    g6: LineSegment StartX=24 StartY=64 StartZ=0 EndX=20 EndY=64 EndZ=0
    g7: LineSegment StartX=20 StartY=64 StartZ=0 EndX=20 EndY=0 EndZ=0
  constraints (23):
    c: Coincident(g0,g1)
    c: Coincident(g1,g2)
    c: Coincident(g2,g3)
    c: Coincident(g3,g0)
    c: Horizontal(g0)
    c: Horizontal(g2)
    c: Vertical(g1)
    c: Vertical(g3)
    c: PointOnObject(g0,g-1)
    c: Coincident(g4,g5)
    c: Coincident(g5,g6)
    c: Coincident(g6,g7)
    c: Coincident(g7,g4)
    c: Horizontal(g4)
    c: Horizontal(g6)
    c: Vertical(g5)
    c: Vertical(g7)
    c: PointOnObject(g4,g-1)
    c: Symmetric(g6,g1,g-2)
    c: Equal(g2,g6)
    c: DistanceX(g0,g0) = 4
    c: DistanceX(g0,g4) = 40
    c: DistanceY(g3,g3) = 64
FEATURE [Part::Extrusion] Extrude027
  Base = -> Sketch022
  Dir = (0,-1,2e-16)
  DirMode = 2
  FaceMakerClass = Part::FaceMakerBullseye
  FaceMakerMode = 3
  LengthFwd = 52
  LengthRev = 0
  Solid = true
  Symmetric = true
  expr: LengthFwd = <<Variables>>.BinWidth + <<Variables>>.WallWidth * 3
FEATURE [Sketcher::SketchObject] Sketch024
  ArcFitTolerance = 1e-06
  FullyConstrained = true
  MakeInternals = false
  Placement = pos=(0,0,0) rot=(1,0,0;1.5708rad)
  expr: Constraints[10] = <<Variables>>.BinWidth * 1.5 + <<Variables>>.WallWidth
  expr: Constraints[9] = <<Variables>>.BinWidth
  sketch-geometry (4):
    g0: LineSegment StartX=-20 StartY=0 StartZ=0 EndX=20 EndY=0 EndZ=0
    g1: LineSegment StartX=20 StartY=0 StartZ=0 EndX=20 EndY=64 EndZ=0
    g2: LineSegment StartX=20 StartY=64 StartZ=0 EndX=-20 EndY=64 EndZ=0
    g3: LineSegment StartX=-20 StartY=64 StartZ=0 EndX=-20 EndY=0 EndZ=0
  constraints (11):
    c: Coincident(g0,g1)
    c: Coincident(g1,g2)
    c: Coincident(g2,g3)
    c: Coincident(g3,g0)
    c: Horizontal(g0)
    c: Vertical(g1)
    c: Vertical(g3)
    c: PointOnObject(g0,g-1)
    c: Symmetric(g2,g1,g-2)
    c: DistanceX(g0,g0) = 40
    c: DistanceY(g3,g3) = 64
FEATURE [Part::Extrusion] Extrude029
  Base = -> Sketch024
  Dir = (0,-1,2e-16)
  DirMode = 2
  FaceMakerClass = Part::FaceMakerBullseye
  FaceMakerMode = 3
  LengthFwd = 0
  LengthRev = 2
  Placement = pos=(0,24,0) rot=(0,0,1;0rad)
  Solid = true
  Symmetric = false
  expr: .Placement.Base.y = <<Variables>>.BinWidth / 2 + <<Variables>>.WallWidth
  expr: LengthRev = <<Variables>>.WallWidth / 2
FEATURE [Sketcher::SketchObject] Sketch025
  ArcFitTolerance = 1e-06
  FullyConstrained = true
  MakeInternals = false
  MapMode = 5
  Placement = pos=(0,0,0) rot=(0.57735,0.57735,0.57735;2.0944rad)
  expr: Constraints[10] = <<Variables>>.BinWidth * 0.75
  expr: Constraints[11] = (<<Variables>>.BinWidth + <<Variables>>.WallWidth) / 2
  expr: Constraints[8] = <<Variables>>.WallWidth / 2
  expr: Constraints[9] = <<Variables>>.BinWidth / 2
  sketch-geometry (4):
    g0: LineSegment StartX=-24 StartY=50 StartZ=0 EndX=-24 EndY=30 EndZ=0
    g1: LineSegment StartX=-24 StartY=30 StartZ=0 EndX=-22 EndY=30 EndZ=0
    g2: LineSegment StartX=-22 StartY=30 StartZ=0 EndX=-22 EndY=50 EndZ=0
    g3: LineSegment StartX=-22 StartY=50 StartZ=0 EndX=-24 EndY=50 EndZ=0
  constraints (12):
    c: Coincident(g0,g1)
    c: Coincident(g1,g2)
    c: Coincident(g2,g3)
    c: Coincident(g3,g0)
    c: Vertical(g0)
    c: Vertical(g2)
    c: Horizontal(g1)
    c: Horizontal(g3)
    c: DistanceX(g3,g3) = 2
    c: DistanceY(g0,g0) = 20
    c: Distance(g0,g-1) = 30
    c: Distance(g1,g-2) = 22
FEATURE [Part::Extrusion] Extrude030
  Base = -> Sketch025
  Dir = (1,0,0)
  DirMode = 2
  FaceMakerClass = Part::FaceMakerBullseye
  FaceMakerMode = 3
  LengthFwd = 40
  LengthRev = 0
  Solid = true
  Symmetric = true
  expr: LengthFwd = <<Variables>>.BinWidth
FEATURE [Sketcher::SketchObject] Sketch026
  ArcFitTolerance = 1e-06
  AttachmentSupport = -> [Sketch025]
  FullyConstrained = true
  MakeInternals = false
  MapMode = 2
  Placement = pos=(0,0,0) rot=(0.57735,0.57735,0.57735;2.0944rad)
  expr: Constraints[10] = <<Variables>>.BinWidth * 1.5 - <<Variables>>.FlapPinDiameter / 2 - <<Variables>>.FlapTolerance
  expr: Constraints[11] = <<Variables>>.BinWidth / 2
  expr: Constraints[8] = <<Variables>>.FlapPinDiameter + <<Variables>>.FlapTolerance
  expr: Constraints[9] = <<Variables>>.BinWidth / 2 + <<Variables>>.WallWidth - <<Variables>>.FlapPinDiameter - <<Variables>>.FlapTolerance
  sketch-geometry (4):
    g0: LineSegment StartX=-15.75 StartY=55.75 StartZ=0 EndX=-15.75 EndY=75.75 EndZ=0
    g1: LineSegment StartX=-15.75 StartY=75.75 StartZ=0 EndX=-24 EndY=75.75 EndZ=0
    g2: LineSegment StartX=-24 StartY=75.75 StartZ=0 EndX=-24 EndY=55.75 EndZ=0
    g3: LineSegment StartX=-24 StartY=55.75 StartZ=0 EndX=-15.75 EndY=55.75 EndZ=0
  constraints (12):
    c: Coincident(g0,g1)
    c: Coincident(g1,g2)
    c: Coincident(g2,g3)
    c: Coincident(g3,g0)
    c: Vertical(g0)
    c: Vertical(g2)
    c: Horizontal(g1)
    c: Horizontal(g3)
    c: DistanceX(g1,g1) = 8.25
    c: Distance(g0,g-2) = 15.75
    c: Distance(g2,g-1) = 55.75
    c: DistanceY(g2,g2) = 20
FEATURE [Part::Extrusion] Extrude031
  Base = -> Sketch026
  Dir = (1,0,0)
  DirMode = 2
  FaceMakerClass = Part::FaceMakerBullseye
  FaceMakerMode = 3
  LengthFwd = 10
  LengthRev = 0
  Placement = pos=(-21.5,0.1,0) rot=(0,0,1;0rad)
  Solid = true
  Symmetric = false
  expr: .Placement.Base.x = <<Variables>>.BinWidth / -2 - <<Variables>>.Tolerance * 1.5
FEATURE [Part::MultiFuse] Fusion010
  Shapes = -> [Extrude028,Extrude031]
FEATURE [Part::MultiFuse] Fusion011
  Shapes = -> [Extrude029,Extrude027,Extrude030]
FEATURE [Part::Cut] Cut005
  Base = -> Fusion011
  Tool = -> Fusion010
